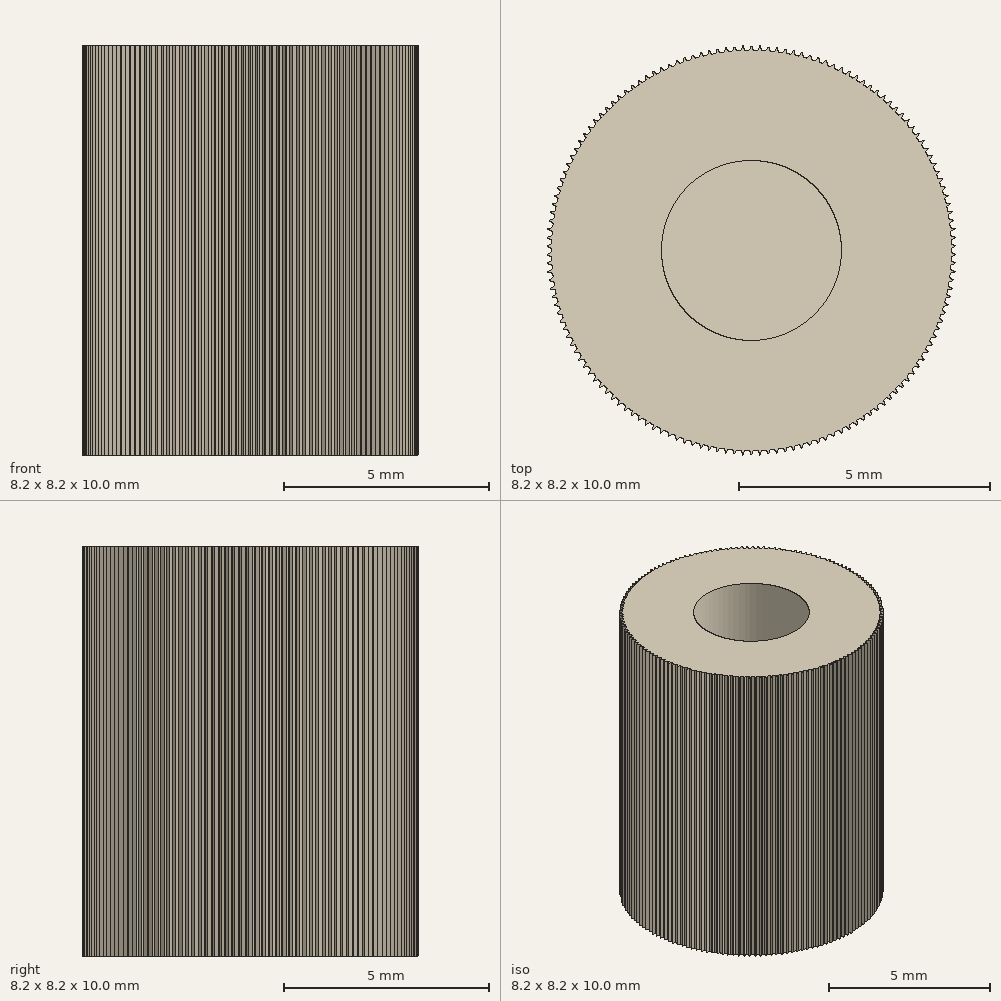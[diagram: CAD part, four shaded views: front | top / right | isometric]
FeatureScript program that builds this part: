
annotation { "Feature Type Name" : "Feature", "Feature Type Description" : "" }
export const myFeature = defineFeature(function(context is Context, id is Id, definition is map)
    precondition{}
    {
        {
            var Q0;
            Q0=qCreatedBy(makeId("Top.planeOp"),FACE);
            var sketch = newSketch(context, id + "F0", { "sketchPlane" : qUnion([Q0])});
            skArc(sketch, "E0", {"start": v(-0.04, 4) * mm, "mid": v(-0.08, 4) * mm, "end": v(-0.13, 4) * mm});
            skLineSegment(sketch, "E1", {"start": v(-0.04, 4) * mm, "end": v(0, 4.1) * mm});
            skLineSegment(sketch, "E2", {"start": v(0, 4.1) * mm, "end": v(0.04, 4) * mm});
            skLineSegment(sketch, "E3.1.0", {"start": v(-0.2, 4) * mm, "end": v(-0.17, 4.1) * mm});
            skLineSegment(sketch, "E3.1.1", {"start": v(-0.17, 4.1) * mm, "end": v(-0.13, 4) * mm});
            skLineSegment(sketch, "E3.2.0", {"start": v(-0.37, 3.98) * mm, "end": v(-0.34, 4.08) * mm});
            skLineSegment(sketch, "E3.2.1", {"start": v(-0.34, 4.08) * mm, "end": v(-0.3, 3.99) * mm});
            skLineSegment(sketch, "E3.3.0", {"start": v(-0.54, 3.96) * mm, "end": v(-0.51, 4.07) * mm});
            skLineSegment(sketch, "E3.3.1", {"start": v(-0.51, 4.07) * mm, "end": v(-0.46, 3.97) * mm});
            skLineSegment(sketch, "E3.4.0", {"start": v(-0.7, 3.94) * mm, "end": v(-0.68, 4.04) * mm});
            skLineSegment(sketch, "E3.4.1", {"start": v(-0.68, 4.04) * mm, "end": v(-0.63, 3.95) * mm});
            skLineSegment(sketch, "E3.5.0", {"start": v(-0.87, 3.9) * mm, "end": v(-0.85, 4) * mm});
            skLineSegment(sketch, "E3.5.1", {"start": v(-0.85, 4) * mm, "end": v(-0.8, 3.92) * mm});
            skLineSegment(sketch, "E3.6.0", {"start": v(-1.03, 3.86) * mm, "end": v(-1.02, 3.97) * mm});
            skLineSegment(sketch, "E3.6.1", {"start": v(-1.02, 3.97) * mm, "end": v(-0.96, 3.88) * mm});
            skLineSegment(sketch, "E3.7.0", {"start": v(-1.2, 3.82) * mm, "end": v(-1.18, 3.92) * mm});
            skLineSegment(sketch, "E3.7.1", {"start": v(-1.18, 3.92) * mm, "end": v(-1.12, 3.84) * mm});
            skLineSegment(sketch, "E3.8.0", {"start": v(-1.35, 3.76) * mm, "end": v(-1.35, 3.87) * mm});
            skLineSegment(sketch, "E3.8.1", {"start": v(-1.35, 3.87) * mm, "end": v(-1.28, 3.8) * mm});
            skLineSegment(sketch, "E3.9.0", {"start": v(-1.5, 3.7) * mm, "end": v(-1.5, 3.81) * mm});
            skLineSegment(sketch, "E3.9.1", {"start": v(-1.5, 3.81) * mm, "end": v(-1.43, 3.73) * mm});
            skLineSegment(sketch, "E3.10.0", {"start": v(-1.66, 3.64) * mm, "end": v(-1.67, 3.74) * mm});
            skLineSegment(sketch, "E3.10.1", {"start": v(-1.67, 3.74) * mm, "end": v(-1.59, 3.67) * mm});
            skLineSegment(sketch, "E3.11.0", {"start": v(-1.81, 3.56) * mm, "end": v(-1.82, 3.67) * mm});
            skLineSegment(sketch, "E3.11.1", {"start": v(-1.82, 3.67) * mm, "end": v(-1.74, 3.6) * mm});
            skLineSegment(sketch, "E3.12.0", {"start": v(-1.96, 3.49) * mm, "end": v(-1.97, 3.6) * mm});
            skLineSegment(sketch, "E3.12.1", {"start": v(-1.97, 3.6) * mm, "end": v(-1.9, 3.52) * mm});
            skLineSegment(sketch, "E3.13.0", {"start": v(-2.1, 3.4) * mm, "end": v(-2.12, 3.5) * mm});
            skLineSegment(sketch, "E3.13.1", {"start": v(-2.12, 3.5) * mm, "end": v(-2.04, 3.44) * mm});
            skLineSegment(sketch, "E3.14.0", {"start": v(-2.25, 3.3) * mm, "end": v(-2.27, 3.41) * mm});
            skLineSegment(sketch, "E3.14.1", {"start": v(-2.27, 3.41) * mm, "end": v(-2.18, 3.35) * mm});
            skLineSegment(sketch, "E3.15.0", {"start": v(-2.38, 3.21) * mm, "end": v(-2.4, 3.32) * mm});
            skLineSegment(sketch, "E3.15.1", {"start": v(-2.4, 3.32) * mm, "end": v(-2.32, 3.26) * mm});
            skLineSegment(sketch, "E3.16.0", {"start": v(-2.52, 3.1) * mm, "end": v(-2.55, 3.21) * mm});
            skLineSegment(sketch, "E3.16.1", {"start": v(-2.55, 3.21) * mm, "end": v(-2.45, 3.16) * mm});
            skLineSegment(sketch, "E3.17.0", {"start": v(-2.64, 3) * mm, "end": v(-2.68, 3.1) * mm});
            skLineSegment(sketch, "E3.17.1", {"start": v(-2.68, 3.1) * mm, "end": v(-2.58, 3.05) * mm});
            skLineSegment(sketch, "E3.18.0", {"start": v(-2.77, 2.89) * mm, "end": v(-2.8, 2.99) * mm});
            skLineSegment(sketch, "E3.18.1", {"start": v(-2.8, 2.99) * mm, "end": v(-2.7, 2.94) * mm});
            skLineSegment(sketch, "E3.19.0", {"start": v(-2.89, 2.77) * mm, "end": v(-2.93, 2.87) * mm});
            skLineSegment(sketch, "E3.19.1", {"start": v(-2.93, 2.87) * mm, "end": v(-2.83, 2.83) * mm});
            skLineSegment(sketch, "E3.20.0", {"start": v(-3, 2.65) * mm, "end": v(-3.05, 2.74) * mm});
            skLineSegment(sketch, "E3.20.1", {"start": v(-3.05, 2.74) * mm, "end": v(-2.95, 2.7) * mm});
            skLineSegment(sketch, "E3.21.0", {"start": v(-3.1, 2.52) * mm, "end": v(-3.16, 2.61) * mm});
            skLineSegment(sketch, "E3.21.1", {"start": v(-3.16, 2.61) * mm, "end": v(-3.06, 2.58) * mm});
            skLineSegment(sketch, "E3.22.0", {"start": v(-3.21, 2.39) * mm, "end": v(-3.26, 2.48) * mm});
            skLineSegment(sketch, "E3.22.1", {"start": v(-3.26, 2.48) * mm, "end": v(-3.16, 2.45) * mm});
            skLineSegment(sketch, "E3.23.0", {"start": v(-3.3, 2.25) * mm, "end": v(-3.37, 2.34) * mm});
            skLineSegment(sketch, "E3.23.1", {"start": v(-3.37, 2.34) * mm, "end": v(-3.26, 2.32) * mm});
            skLineSegment(sketch, "E3.24.0", {"start": v(-3.4, 2.1) * mm, "end": v(-3.46, 2.2) * mm});
            skLineSegment(sketch, "E3.24.1", {"start": v(-3.46, 2.2) * mm, "end": v(-3.36, 2.18) * mm});
            skLineSegment(sketch, "E3.25.0", {"start": v(-3.48, 1.97) * mm, "end": v(-3.55, 2.05) * mm});
            skLineSegment(sketch, "E3.25.1", {"start": v(-3.55, 2.05) * mm, "end": v(-3.44, 2.04) * mm});
            skLineSegment(sketch, "E3.26.0", {"start": v(-3.56, 1.82) * mm, "end": v(-3.63, 1.9) * mm});
            skLineSegment(sketch, "E3.26.1", {"start": v(-3.63, 1.9) * mm, "end": v(-3.53, 1.89) * mm});
            skLineSegment(sketch, "E3.27.0", {"start": v(-3.64, 1.67) * mm, "end": v(-3.7, 1.75) * mm});
            skLineSegment(sketch, "E3.27.1", {"start": v(-3.7, 1.75) * mm, "end": v(-3.6, 1.74) * mm});
            skLineSegment(sketch, "E3.28.0", {"start": v(-3.7, 1.51) * mm, "end": v(-3.78, 1.59) * mm});
            skLineSegment(sketch, "E3.28.1", {"start": v(-3.78, 1.59) * mm, "end": v(-3.67, 1.59) * mm});
            skLineSegment(sketch, "E3.29.0", {"start": v(-3.76, 1.36) * mm, "end": v(-3.84, 1.43) * mm});
            skLineSegment(sketch, "E3.29.1", {"start": v(-3.84, 1.43) * mm, "end": v(-3.73, 1.43) * mm});
            skLineSegment(sketch, "E3.30.0", {"start": v(-3.82, 1.2) * mm, "end": v(-3.9, 1.27) * mm});
            skLineSegment(sketch, "E3.30.1", {"start": v(-3.9, 1.27) * mm, "end": v(-3.8, 1.27) * mm});
            skLineSegment(sketch, "E3.31.0", {"start": v(-3.86, 1.04) * mm, "end": v(-3.95, 1.1) * mm});
            skLineSegment(sketch, "E3.31.1", {"start": v(-3.95, 1.1) * mm, "end": v(-3.84, 1.11) * mm});
            skLineSegment(sketch, "E3.32.0", {"start": v(-3.9, 0.87) * mm, "end": v(-4, 0.94) * mm});
            skLineSegment(sketch, "E3.32.1", {"start": v(-4, 0.94) * mm, "end": v(-3.88, 0.95) * mm});
            skLineSegment(sketch, "E3.33.0", {"start": v(-3.94, 0.71) * mm, "end": v(-4.03, 0.77) * mm});
            skLineSegment(sketch, "E3.33.1", {"start": v(-4.03, 0.77) * mm, "end": v(-3.92, 0.79) * mm});
            skLineSegment(sketch, "E3.34.0", {"start": v(-3.96, 0.54) * mm, "end": v(-4.05, 0.6) * mm});
            skLineSegment(sketch, "E3.34.1", {"start": v(-4.05, 0.6) * mm, "end": v(-3.95, 0.62) * mm});
            skLineSegment(sketch, "E3.35.0", {"start": v(-3.98, 0.38) * mm, "end": v(-4.08, 0.43) * mm});
            skLineSegment(sketch, "E3.35.1", {"start": v(-4.08, 0.43) * mm, "end": v(-3.97, 0.46) * mm});
            skLineSegment(sketch, "E3.36.0", {"start": v(-4, 0.21) * mm, "end": v(-4.1, 0.26) * mm});
            skLineSegment(sketch, "E3.36.1", {"start": v(-4.1, 0.26) * mm, "end": v(-3.99, 0.3) * mm});
            skLineSegment(sketch, "E3.37.0", {"start": v(-4, 0.04) * mm, "end": v(-4.1, 0.09) * mm});
            skLineSegment(sketch, "E3.37.1", {"start": v(-4.1, 0.09) * mm, "end": v(-4, 0.12) * mm});
            skLineSegment(sketch, "E3.38.0", {"start": v(-4, -0.12) * mm, "end": v(-4.1, -0.09) * mm});
            skLineSegment(sketch, "E3.38.1", {"start": v(-4.1, -0.09) * mm, "end": v(-4, -0.04) * mm});
            skLineSegment(sketch, "E3.39.0", {"start": v(-3.99, -0.3) * mm, "end": v(-4.1, -0.26) * mm});
            skLineSegment(sketch, "E3.39.1", {"start": v(-4.1, -0.26) * mm, "end": v(-4, -0.21) * mm});
            skLineSegment(sketch, "E3.40.0", {"start": v(-3.97, -0.46) * mm, "end": v(-4.08, -0.43) * mm});
            skLineSegment(sketch, "E3.40.1", {"start": v(-4.08, -0.43) * mm, "end": v(-3.98, -0.38) * mm});
            skLineSegment(sketch, "E3.41.0", {"start": v(-3.95, -0.62) * mm, "end": v(-4.05, -0.6) * mm});
            skLineSegment(sketch, "E3.41.1", {"start": v(-4.05, -0.6) * mm, "end": v(-3.96, -0.54) * mm});
            skLineSegment(sketch, "E3.42.0", {"start": v(-3.92, -0.79) * mm, "end": v(-4.03, -0.77) * mm});
            skLineSegment(sketch, "E3.42.1", {"start": v(-4.03, -0.77) * mm, "end": v(-3.94, -0.7) * mm});
            skLineSegment(sketch, "E3.43.0", {"start": v(-3.88, -0.95) * mm, "end": v(-4, -0.94) * mm});
            skLineSegment(sketch, "E3.43.1", {"start": v(-4, -0.94) * mm, "end": v(-3.9, -0.87) * mm});
            skLineSegment(sketch, "E3.44.0", {"start": v(-3.84, -1.11) * mm, "end": v(-3.95, -1.1) * mm});
            skLineSegment(sketch, "E3.44.1", {"start": v(-3.95, -1.1) * mm, "end": v(-3.86, -1.04) * mm});
            skLineSegment(sketch, "E3.45.0", {"start": v(-3.8, -1.27) * mm, "end": v(-3.9, -1.27) * mm});
            skLineSegment(sketch, "E3.45.1", {"start": v(-3.9, -1.27) * mm, "end": v(-3.82, -1.2) * mm});
            skLineSegment(sketch, "E3.46.0", {"start": v(-3.73, -1.43) * mm, "end": v(-3.84, -1.43) * mm});
            skLineSegment(sketch, "E3.46.1", {"start": v(-3.84, -1.43) * mm, "end": v(-3.76, -1.36) * mm});
            skLineSegment(sketch, "E3.47.0", {"start": v(-3.67, -1.59) * mm, "end": v(-3.78, -1.59) * mm});
            skLineSegment(sketch, "E3.47.1", {"start": v(-3.78, -1.59) * mm, "end": v(-3.7, -1.51) * mm});
            skLineSegment(sketch, "E3.48.0", {"start": v(-3.6, -1.74) * mm, "end": v(-3.7, -1.75) * mm});
            skLineSegment(sketch, "E3.48.1", {"start": v(-3.7, -1.75) * mm, "end": v(-3.64, -1.67) * mm});
            skLineSegment(sketch, "E3.49.0", {"start": v(-3.53, -1.89) * mm, "end": v(-3.63, -1.9) * mm});
            skLineSegment(sketch, "E3.49.1", {"start": v(-3.63, -1.9) * mm, "end": v(-3.56, -1.82) * mm});
            skLineSegment(sketch, "E3.50.0", {"start": v(-3.44, -2.03) * mm, "end": v(-3.55, -2.05) * mm});
            skLineSegment(sketch, "E3.50.1", {"start": v(-3.55, -2.05) * mm, "end": v(-3.48, -1.96) * mm});
            skLineSegment(sketch, "E3.51.0", {"start": v(-3.36, -2.18) * mm, "end": v(-3.46, -2.2) * mm});
            skLineSegment(sketch, "E3.51.1", {"start": v(-3.46, -2.2) * mm, "end": v(-3.4, -2.1) * mm});
            skLineSegment(sketch, "E3.52.0", {"start": v(-3.26, -2.32) * mm, "end": v(-3.37, -2.34) * mm});
            skLineSegment(sketch, "E3.52.1", {"start": v(-3.37, -2.34) * mm, "end": v(-3.3, -2.25) * mm});
            skLineSegment(sketch, "E3.53.0", {"start": v(-3.16, -2.45) * mm, "end": v(-3.26, -2.48) * mm});
            skLineSegment(sketch, "E3.53.1", {"start": v(-3.26, -2.48) * mm, "end": v(-3.21, -2.39) * mm});
            skLineSegment(sketch, "E3.54.0", {"start": v(-3.06, -2.58) * mm, "end": v(-3.16, -2.61) * mm});
            skLineSegment(sketch, "E3.54.1", {"start": v(-3.16, -2.61) * mm, "end": v(-3.1, -2.52) * mm});
            skLineSegment(sketch, "E3.55.0", {"start": v(-2.95, -2.7) * mm, "end": v(-3.05, -2.74) * mm});
            skLineSegment(sketch, "E3.55.1", {"start": v(-3.05, -2.74) * mm, "end": v(-3, -2.65) * mm});
            skLineSegment(sketch, "E3.56.0", {"start": v(-2.83, -2.83) * mm, "end": v(-2.93, -2.87) * mm});
            skLineSegment(sketch, "E3.56.1", {"start": v(-2.93, -2.87) * mm, "end": v(-2.89, -2.77) * mm});
            skLineSegment(sketch, "E3.57.0", {"start": v(-2.7, -2.94) * mm, "end": v(-2.8, -2.99) * mm});
            skLineSegment(sketch, "E3.57.1", {"start": v(-2.8, -2.99) * mm, "end": v(-2.77, -2.89) * mm});
            skLineSegment(sketch, "E3.58.0", {"start": v(-2.58, -3.05) * mm, "end": v(-2.68, -3.1) * mm});
            skLineSegment(sketch, "E3.58.1", {"start": v(-2.68, -3.1) * mm, "end": v(-2.64, -3) * mm});
            skLineSegment(sketch, "E3.59.0", {"start": v(-2.45, -3.16) * mm, "end": v(-2.55, -3.21) * mm});
            skLineSegment(sketch, "E3.59.1", {"start": v(-2.55, -3.21) * mm, "end": v(-2.52, -3.1) * mm});
            skLineSegment(sketch, "E3.60.0", {"start": v(-2.32, -3.26) * mm, "end": v(-2.4, -3.32) * mm});
            skLineSegment(sketch, "E3.60.1", {"start": v(-2.4, -3.32) * mm, "end": v(-2.38, -3.21) * mm});
            skLineSegment(sketch, "E3.61.0", {"start": v(-2.18, -3.35) * mm, "end": v(-2.27, -3.41) * mm});
            skLineSegment(sketch, "E3.61.1", {"start": v(-2.27, -3.41) * mm, "end": v(-2.25, -3.3) * mm});
            skLineSegment(sketch, "E3.62.0", {"start": v(-2.04, -3.44) * mm, "end": v(-2.12, -3.5) * mm});
            skLineSegment(sketch, "E3.62.1", {"start": v(-2.12, -3.5) * mm, "end": v(-2.1, -3.4) * mm});
            skLineSegment(sketch, "E3.63.0", {"start": v(-1.9, -3.52) * mm, "end": v(-1.97, -3.6) * mm});
            skLineSegment(sketch, "E3.63.1", {"start": v(-1.97, -3.6) * mm, "end": v(-1.96, -3.49) * mm});
            skLineSegment(sketch, "E3.64.0", {"start": v(-1.74, -3.6) * mm, "end": v(-1.82, -3.67) * mm});
            skLineSegment(sketch, "E3.64.1", {"start": v(-1.82, -3.67) * mm, "end": v(-1.81, -3.56) * mm});
            skLineSegment(sketch, "E3.65.0", {"start": v(-1.6, -3.67) * mm, "end": v(-1.67, -3.74) * mm});
            skLineSegment(sketch, "E3.65.1", {"start": v(-1.67, -3.74) * mm, "end": v(-1.66, -3.64) * mm});
            skLineSegment(sketch, "E3.66.0", {"start": v(-1.44, -3.73) * mm, "end": v(-1.5, -3.81) * mm});
            skLineSegment(sketch, "E3.66.1", {"start": v(-1.5, -3.81) * mm, "end": v(-1.51, -3.7) * mm});
            skLineSegment(sketch, "E3.67.0", {"start": v(-1.28, -3.8) * mm, "end": v(-1.35, -3.87) * mm});
            skLineSegment(sketch, "E3.67.1", {"start": v(-1.35, -3.87) * mm, "end": v(-1.35, -3.76) * mm});
            skLineSegment(sketch, "E3.68.0", {"start": v(-1.12, -3.84) * mm, "end": v(-1.18, -3.92) * mm});
            skLineSegment(sketch, "E3.68.1", {"start": v(-1.18, -3.92) * mm, "end": v(-1.2, -3.82) * mm});
            skLineSegment(sketch, "E3.69.0", {"start": v(-0.96, -3.88) * mm, "end": v(-1.02, -3.97) * mm});
            skLineSegment(sketch, "E3.69.1", {"start": v(-1.02, -3.97) * mm, "end": v(-1.03, -3.86) * mm});
            skLineSegment(sketch, "E3.70.0", {"start": v(-0.8, -3.92) * mm, "end": v(-0.85, -4) * mm});
            skLineSegment(sketch, "E3.70.1", {"start": v(-0.85, -4) * mm, "end": v(-0.87, -3.9) * mm});
            skLineSegment(sketch, "E3.71.0", {"start": v(-0.63, -3.95) * mm, "end": v(-0.68, -4.04) * mm});
            skLineSegment(sketch, "E3.71.1", {"start": v(-0.68, -4.04) * mm, "end": v(-0.7, -3.94) * mm});
            skLineSegment(sketch, "E3.72.0", {"start": v(-0.46, -3.97) * mm, "end": v(-0.51, -4.07) * mm});
            skLineSegment(sketch, "E3.72.1", {"start": v(-0.51, -4.07) * mm, "end": v(-0.54, -3.96) * mm});
            skLineSegment(sketch, "E3.73.0", {"start": v(-0.3, -3.99) * mm, "end": v(-0.34, -4.08) * mm});
            skLineSegment(sketch, "E3.73.1", {"start": v(-0.34, -4.08) * mm, "end": v(-0.38, -3.98) * mm});
            skLineSegment(sketch, "E3.74.0", {"start": v(-0.13, -4) * mm, "end": v(-0.17, -4.1) * mm});
            skLineSegment(sketch, "E3.74.1", {"start": v(-0.17, -4.1) * mm, "end": v(-0.2, -4) * mm});
            skLineSegment(sketch, "E3.75.0", {"start": v(0.04, -4) * mm, "end": v(0, -4.1) * mm});
            skLineSegment(sketch, "E3.75.1", {"start": v(0, -4.1) * mm, "end": v(-0.04, -4) * mm});
            skLineSegment(sketch, "E3.76.0", {"start": v(0.2, -4) * mm, "end": v(0.17, -4.1) * mm});
            skLineSegment(sketch, "E3.76.1", {"start": v(0.17, -4.1) * mm, "end": v(0.13, -4) * mm});
            skLineSegment(sketch, "E3.77.0", {"start": v(0.37, -3.98) * mm, "end": v(0.34, -4.08) * mm});
            skLineSegment(sketch, "E3.77.1", {"start": v(0.34, -4.08) * mm, "end": v(0.3, -3.99) * mm});
            skLineSegment(sketch, "E3.78.0", {"start": v(0.54, -3.96) * mm, "end": v(0.51, -4.07) * mm});
            skLineSegment(sketch, "E3.78.1", {"start": v(0.51, -4.07) * mm, "end": v(0.46, -3.97) * mm});
            skLineSegment(sketch, "E3.79.0", {"start": v(0.7, -3.94) * mm, "end": v(0.68, -4.04) * mm});
            skLineSegment(sketch, "E3.79.1", {"start": v(0.68, -4.04) * mm, "end": v(0.63, -3.95) * mm});
            skLineSegment(sketch, "E3.80.0", {"start": v(0.87, -3.9) * mm, "end": v(0.85, -4) * mm});
            skLineSegment(sketch, "E3.80.1", {"start": v(0.85, -4) * mm, "end": v(0.8, -3.92) * mm});
            skLineSegment(sketch, "E3.81.0", {"start": v(1.03, -3.86) * mm, "end": v(1.02, -3.97) * mm});
            skLineSegment(sketch, "E3.81.1", {"start": v(1.02, -3.97) * mm, "end": v(0.96, -3.88) * mm});
            skLineSegment(sketch, "E3.82.0", {"start": v(1.2, -3.82) * mm, "end": v(1.18, -3.92) * mm});
            skLineSegment(sketch, "E3.82.1", {"start": v(1.18, -3.92) * mm, "end": v(1.12, -3.84) * mm});
            skLineSegment(sketch, "E3.83.0", {"start": v(1.35, -3.76) * mm, "end": v(1.35, -3.87) * mm});
            skLineSegment(sketch, "E3.83.1", {"start": v(1.35, -3.87) * mm, "end": v(1.28, -3.8) * mm});
            skLineSegment(sketch, "E3.84.0", {"start": v(1.5, -3.7) * mm, "end": v(1.5, -3.81) * mm});
            skLineSegment(sketch, "E3.84.1", {"start": v(1.5, -3.81) * mm, "end": v(1.43, -3.73) * mm});
            skLineSegment(sketch, "E3.85.0", {"start": v(1.66, -3.64) * mm, "end": v(1.67, -3.74) * mm});
            skLineSegment(sketch, "E3.85.1", {"start": v(1.67, -3.74) * mm, "end": v(1.59, -3.67) * mm});
            skLineSegment(sketch, "E3.86.0", {"start": v(1.81, -3.56) * mm, "end": v(1.82, -3.67) * mm});
            skLineSegment(sketch, "E3.86.1", {"start": v(1.82, -3.67) * mm, "end": v(1.74, -3.6) * mm});
            skLineSegment(sketch, "E3.87.0", {"start": v(1.96, -3.49) * mm, "end": v(1.97, -3.6) * mm});
            skLineSegment(sketch, "E3.87.1", {"start": v(1.97, -3.6) * mm, "end": v(1.9, -3.52) * mm});
            skLineSegment(sketch, "E3.88.0", {"start": v(2.1, -3.4) * mm, "end": v(2.12, -3.5) * mm});
            skLineSegment(sketch, "E3.88.1", {"start": v(2.12, -3.5) * mm, "end": v(2.04, -3.44) * mm});
            skLineSegment(sketch, "E3.89.0", {"start": v(2.25, -3.3) * mm, "end": v(2.27, -3.41) * mm});
            skLineSegment(sketch, "E3.89.1", {"start": v(2.27, -3.41) * mm, "end": v(2.18, -3.35) * mm});
            skLineSegment(sketch, "E3.90.0", {"start": v(2.38, -3.21) * mm, "end": v(2.4, -3.32) * mm});
            skLineSegment(sketch, "E3.90.1", {"start": v(2.4, -3.32) * mm, "end": v(2.32, -3.26) * mm});
            skLineSegment(sketch, "E3.91.0", {"start": v(2.52, -3.1) * mm, "end": v(2.55, -3.21) * mm});
            skLineSegment(sketch, "E3.91.1", {"start": v(2.55, -3.21) * mm, "end": v(2.45, -3.16) * mm});
            skLineSegment(sketch, "E3.92.0", {"start": v(2.64, -3) * mm, "end": v(2.68, -3.1) * mm});
            skLineSegment(sketch, "E3.92.1", {"start": v(2.68, -3.1) * mm, "end": v(2.58, -3.05) * mm});
            skLineSegment(sketch, "E3.93.0", {"start": v(2.77, -2.89) * mm, "end": v(2.8, -2.99) * mm});
            skLineSegment(sketch, "E3.93.1", {"start": v(2.8, -2.99) * mm, "end": v(2.7, -2.94) * mm});
            skLineSegment(sketch, "E3.94.0", {"start": v(2.89, -2.77) * mm, "end": v(2.93, -2.87) * mm});
            skLineSegment(sketch, "E3.94.1", {"start": v(2.93, -2.87) * mm, "end": v(2.83, -2.83) * mm});
            skLineSegment(sketch, "E3.95.0", {"start": v(3, -2.65) * mm, "end": v(3.05, -2.74) * mm});
            skLineSegment(sketch, "E3.95.1", {"start": v(3.05, -2.74) * mm, "end": v(2.95, -2.7) * mm});
            skLineSegment(sketch, "E3.96.0", {"start": v(3.1, -2.52) * mm, "end": v(3.16, -2.61) * mm});
            skLineSegment(sketch, "E3.96.1", {"start": v(3.16, -2.61) * mm, "end": v(3.06, -2.58) * mm});
            skLineSegment(sketch, "E3.97.0", {"start": v(3.21, -2.39) * mm, "end": v(3.26, -2.48) * mm});
            skLineSegment(sketch, "E3.97.1", {"start": v(3.26, -2.48) * mm, "end": v(3.16, -2.45) * mm});
            skLineSegment(sketch, "E3.98.0", {"start": v(3.3, -2.25) * mm, "end": v(3.37, -2.34) * mm});
            skLineSegment(sketch, "E3.98.1", {"start": v(3.37, -2.34) * mm, "end": v(3.26, -2.32) * mm});
            skLineSegment(sketch, "E3.99.0", {"start": v(3.4, -2.1) * mm, "end": v(3.46, -2.2) * mm});
            skLineSegment(sketch, "E3.99.1", {"start": v(3.46, -2.2) * mm, "end": v(3.36, -2.18) * mm});
            skLineSegment(sketch, "E3.100.0", {"start": v(3.48, -1.97) * mm, "end": v(3.55, -2.05) * mm});
            skLineSegment(sketch, "E3.100.1", {"start": v(3.55, -2.05) * mm, "end": v(3.44, -2.04) * mm});
            skLineSegment(sketch, "E3.101.0", {"start": v(3.56, -1.82) * mm, "end": v(3.63, -1.9) * mm});
            skLineSegment(sketch, "E3.101.1", {"start": v(3.63, -1.9) * mm, "end": v(3.53, -1.89) * mm});
            skLineSegment(sketch, "E3.102.0", {"start": v(3.64, -1.67) * mm, "end": v(3.7, -1.75) * mm});
            skLineSegment(sketch, "E3.102.1", {"start": v(3.7, -1.75) * mm, "end": v(3.6, -1.74) * mm});
            skLineSegment(sketch, "E3.103.0", {"start": v(3.7, -1.51) * mm, "end": v(3.78, -1.59) * mm});
            skLineSegment(sketch, "E3.103.1", {"start": v(3.78, -1.59) * mm, "end": v(3.67, -1.59) * mm});
            skLineSegment(sketch, "E3.104.0", {"start": v(3.76, -1.36) * mm, "end": v(3.84, -1.43) * mm});
            skLineSegment(sketch, "E3.104.1", {"start": v(3.84, -1.43) * mm, "end": v(3.73, -1.43) * mm});
            skLineSegment(sketch, "E3.105.0", {"start": v(3.82, -1.2) * mm, "end": v(3.9, -1.27) * mm});
            skLineSegment(sketch, "E3.105.1", {"start": v(3.9, -1.27) * mm, "end": v(3.8, -1.27) * mm});
            skLineSegment(sketch, "E3.106.0", {"start": v(3.86, -1.04) * mm, "end": v(3.95, -1.1) * mm});
            skLineSegment(sketch, "E3.106.1", {"start": v(3.95, -1.1) * mm, "end": v(3.84, -1.11) * mm});
            skLineSegment(sketch, "E3.107.0", {"start": v(3.9, -0.87) * mm, "end": v(4, -0.94) * mm});
            skLineSegment(sketch, "E3.107.1", {"start": v(4, -0.94) * mm, "end": v(3.88, -0.95) * mm});
            skLineSegment(sketch, "E3.108.0", {"start": v(3.94, -0.71) * mm, "end": v(4.03, -0.77) * mm});
            skLineSegment(sketch, "E3.108.1", {"start": v(4.03, -0.77) * mm, "end": v(3.92, -0.79) * mm});
            skLineSegment(sketch, "E3.109.0", {"start": v(3.96, -0.54) * mm, "end": v(4.05, -0.6) * mm});
            skLineSegment(sketch, "E3.109.1", {"start": v(4.05, -0.6) * mm, "end": v(3.95, -0.62) * mm});
            skLineSegment(sketch, "E3.110.0", {"start": v(3.98, -0.38) * mm, "end": v(4.08, -0.43) * mm});
            skLineSegment(sketch, "E3.110.1", {"start": v(4.08, -0.43) * mm, "end": v(3.97, -0.46) * mm});
            skLineSegment(sketch, "E3.111.0", {"start": v(4, -0.21) * mm, "end": v(4.1, -0.26) * mm});
            skLineSegment(sketch, "E3.111.1", {"start": v(4.1, -0.26) * mm, "end": v(3.99, -0.3) * mm});
            skLineSegment(sketch, "E3.112.0", {"start": v(4, -0.04) * mm, "end": v(4.1, -0.09) * mm});
            skLineSegment(sketch, "E3.112.1", {"start": v(4.1, -0.09) * mm, "end": v(4, -0.12) * mm});
            skLineSegment(sketch, "E3.113.0", {"start": v(4, 0.12) * mm, "end": v(4.1, 0.09) * mm});
            skLineSegment(sketch, "E3.113.1", {"start": v(4.1, 0.09) * mm, "end": v(4, 0.04) * mm});
            skLineSegment(sketch, "E3.114.0", {"start": v(3.99, 0.3) * mm, "end": v(4.1, 0.26) * mm});
            skLineSegment(sketch, "E3.114.1", {"start": v(4.1, 0.26) * mm, "end": v(4, 0.21) * mm});
            skLineSegment(sketch, "E3.115.0", {"start": v(3.97, 0.46) * mm, "end": v(4.08, 0.43) * mm});
            skLineSegment(sketch, "E3.115.1", {"start": v(4.08, 0.43) * mm, "end": v(3.98, 0.38) * mm});
            skLineSegment(sketch, "E3.116.0", {"start": v(3.95, 0.62) * mm, "end": v(4.05, 0.6) * mm});
            skLineSegment(sketch, "E3.116.1", {"start": v(4.05, 0.6) * mm, "end": v(3.96, 0.54) * mm});
            skLineSegment(sketch, "E3.117.0", {"start": v(3.92, 0.79) * mm, "end": v(4.03, 0.77) * mm});
            skLineSegment(sketch, "E3.117.1", {"start": v(4.03, 0.77) * mm, "end": v(3.94, 0.7) * mm});
            skLineSegment(sketch, "E3.118.0", {"start": v(3.88, 0.95) * mm, "end": v(4, 0.94) * mm});
            skLineSegment(sketch, "E3.118.1", {"start": v(4, 0.94) * mm, "end": v(3.9, 0.87) * mm});
            skLineSegment(sketch, "E3.119.0", {"start": v(3.84, 1.11) * mm, "end": v(3.95, 1.1) * mm});
            skLineSegment(sketch, "E3.119.1", {"start": v(3.95, 1.1) * mm, "end": v(3.86, 1.04) * mm});
            skLineSegment(sketch, "E3.120.0", {"start": v(3.8, 1.27) * mm, "end": v(3.9, 1.27) * mm});
            skLineSegment(sketch, "E3.120.1", {"start": v(3.9, 1.27) * mm, "end": v(3.82, 1.2) * mm});
            skLineSegment(sketch, "E3.121.0", {"start": v(3.73, 1.43) * mm, "end": v(3.84, 1.43) * mm});
            skLineSegment(sketch, "E3.121.1", {"start": v(3.84, 1.43) * mm, "end": v(3.76, 1.36) * mm});
            skLineSegment(sketch, "E3.122.0", {"start": v(3.67, 1.59) * mm, "end": v(3.78, 1.59) * mm});
            skLineSegment(sketch, "E3.122.1", {"start": v(3.78, 1.59) * mm, "end": v(3.7, 1.51) * mm});
            skLineSegment(sketch, "E3.123.0", {"start": v(3.6, 1.74) * mm, "end": v(3.7, 1.75) * mm});
            skLineSegment(sketch, "E3.123.1", {"start": v(3.7, 1.75) * mm, "end": v(3.64, 1.67) * mm});
            skLineSegment(sketch, "E3.124.0", {"start": v(3.53, 1.89) * mm, "end": v(3.63, 1.9) * mm});
            skLineSegment(sketch, "E3.124.1", {"start": v(3.63, 1.9) * mm, "end": v(3.56, 1.82) * mm});
            skLineSegment(sketch, "E3.125.0", {"start": v(3.44, 2.03) * mm, "end": v(3.55, 2.05) * mm});
            skLineSegment(sketch, "E3.125.1", {"start": v(3.55, 2.05) * mm, "end": v(3.48, 1.96) * mm});
            skLineSegment(sketch, "E3.126.0", {"start": v(3.36, 2.18) * mm, "end": v(3.46, 2.2) * mm});
            skLineSegment(sketch, "E3.126.1", {"start": v(3.46, 2.2) * mm, "end": v(3.4, 2.1) * mm});
            skLineSegment(sketch, "E3.127.0", {"start": v(3.26, 2.32) * mm, "end": v(3.37, 2.34) * mm});
            skLineSegment(sketch, "E3.127.1", {"start": v(3.37, 2.34) * mm, "end": v(3.3, 2.25) * mm});
            skLineSegment(sketch, "E3.128.0", {"start": v(3.16, 2.45) * mm, "end": v(3.26, 2.48) * mm});
            skLineSegment(sketch, "E3.128.1", {"start": v(3.26, 2.48) * mm, "end": v(3.21, 2.39) * mm});
            skLineSegment(sketch, "E3.129.0", {"start": v(3.06, 2.58) * mm, "end": v(3.16, 2.61) * mm});
            skLineSegment(sketch, "E3.129.1", {"start": v(3.16, 2.61) * mm, "end": v(3.1, 2.52) * mm});
            skLineSegment(sketch, "E3.130.0", {"start": v(2.95, 2.7) * mm, "end": v(3.05, 2.74) * mm});
            skLineSegment(sketch, "E3.130.1", {"start": v(3.05, 2.74) * mm, "end": v(3, 2.65) * mm});
            skLineSegment(sketch, "E3.131.0", {"start": v(2.83, 2.83) * mm, "end": v(2.93, 2.87) * mm});
            skLineSegment(sketch, "E3.131.1", {"start": v(2.93, 2.87) * mm, "end": v(2.89, 2.77) * mm});
            skLineSegment(sketch, "E3.132.0", {"start": v(2.7, 2.94) * mm, "end": v(2.8, 2.99) * mm});
            skLineSegment(sketch, "E3.132.1", {"start": v(2.8, 2.99) * mm, "end": v(2.77, 2.89) * mm});
            skLineSegment(sketch, "E3.133.0", {"start": v(2.58, 3.05) * mm, "end": v(2.68, 3.1) * mm});
            skLineSegment(sketch, "E3.133.1", {"start": v(2.68, 3.1) * mm, "end": v(2.64, 3) * mm});
            skLineSegment(sketch, "E3.134.0", {"start": v(2.45, 3.16) * mm, "end": v(2.55, 3.21) * mm});
            skLineSegment(sketch, "E3.134.1", {"start": v(2.55, 3.21) * mm, "end": v(2.52, 3.1) * mm});
            skLineSegment(sketch, "E3.135.0", {"start": v(2.32, 3.26) * mm, "end": v(2.4, 3.32) * mm});
            skLineSegment(sketch, "E3.135.1", {"start": v(2.4, 3.32) * mm, "end": v(2.38, 3.21) * mm});
            skLineSegment(sketch, "E3.136.0", {"start": v(2.18, 3.35) * mm, "end": v(2.27, 3.41) * mm});
            skLineSegment(sketch, "E3.136.1", {"start": v(2.27, 3.41) * mm, "end": v(2.25, 3.3) * mm});
            skLineSegment(sketch, "E3.137.0", {"start": v(2.04, 3.44) * mm, "end": v(2.12, 3.5) * mm});
            skLineSegment(sketch, "E3.137.1", {"start": v(2.12, 3.5) * mm, "end": v(2.1, 3.4) * mm});
            skLineSegment(sketch, "E3.138.0", {"start": v(1.9, 3.52) * mm, "end": v(1.97, 3.6) * mm});
            skLineSegment(sketch, "E3.138.1", {"start": v(1.97, 3.6) * mm, "end": v(1.96, 3.49) * mm});
            skLineSegment(sketch, "E3.139.0", {"start": v(1.74, 3.6) * mm, "end": v(1.82, 3.67) * mm});
            skLineSegment(sketch, "E3.139.1", {"start": v(1.82, 3.67) * mm, "end": v(1.81, 3.56) * mm});
            skLineSegment(sketch, "E3.140.0", {"start": v(1.6, 3.67) * mm, "end": v(1.67, 3.74) * mm});
            skLineSegment(sketch, "E3.140.1", {"start": v(1.67, 3.74) * mm, "end": v(1.66, 3.64) * mm});
            skLineSegment(sketch, "E3.141.0", {"start": v(1.44, 3.73) * mm, "end": v(1.5, 3.81) * mm});
            skLineSegment(sketch, "E3.141.1", {"start": v(1.5, 3.81) * mm, "end": v(1.51, 3.7) * mm});
            skLineSegment(sketch, "E3.142.0", {"start": v(1.28, 3.8) * mm, "end": v(1.35, 3.87) * mm});
            skLineSegment(sketch, "E3.142.1", {"start": v(1.35, 3.87) * mm, "end": v(1.35, 3.76) * mm});
            skLineSegment(sketch, "E3.143.0", {"start": v(1.12, 3.84) * mm, "end": v(1.18, 3.92) * mm});
            skLineSegment(sketch, "E3.143.1", {"start": v(1.18, 3.92) * mm, "end": v(1.2, 3.82) * mm});
            skLineSegment(sketch, "E3.144.0", {"start": v(0.96, 3.88) * mm, "end": v(1.02, 3.97) * mm});
            skLineSegment(sketch, "E3.144.1", {"start": v(1.02, 3.97) * mm, "end": v(1.03, 3.86) * mm});
            skLineSegment(sketch, "E3.145.0", {"start": v(0.8, 3.92) * mm, "end": v(0.85, 4) * mm});
            skLineSegment(sketch, "E3.145.1", {"start": v(0.85, 4) * mm, "end": v(0.87, 3.9) * mm});
            skLineSegment(sketch, "E3.146.0", {"start": v(0.63, 3.95) * mm, "end": v(0.68, 4.04) * mm});
            skLineSegment(sketch, "E3.146.1", {"start": v(0.68, 4.04) * mm, "end": v(0.7, 3.94) * mm});
            skLineSegment(sketch, "E3.147.0", {"start": v(0.46, 3.97) * mm, "end": v(0.51, 4.07) * mm});
            skLineSegment(sketch, "E3.147.1", {"start": v(0.51, 4.07) * mm, "end": v(0.54, 3.96) * mm});
            skLineSegment(sketch, "E3.148.0", {"start": v(0.3, 3.99) * mm, "end": v(0.34, 4.08) * mm});
            skLineSegment(sketch, "E3.148.1", {"start": v(0.34, 4.08) * mm, "end": v(0.38, 3.98) * mm});
            skLineSegment(sketch, "E3.149.0", {"start": v(0.13, 4) * mm, "end": v(0.17, 4.1) * mm});
            skLineSegment(sketch, "E3.149.1", {"start": v(0.17, 4.1) * mm, "end": v(0.2, 4) * mm});
            skArc(sketch, "E4.trimOffspring", {"start": v(0.13, 4) * mm, "mid": v(0.08, 4) * mm, "end": v(0.04, 4) * mm});
            skArc(sketch, "E5.trimOffspring", {"start": v(0.3, 3.99) * mm, "mid": v(0.25, 4) * mm, "end": v(0.2, 4) * mm});
            skArc(sketch, "E6.trimOffspring", {"start": v(0.46, 3.97) * mm, "mid": v(0.42, 3.98) * mm, "end": v(0.38, 3.98) * mm});
            skArc(sketch, "E7.trimOffspring", {"start": v(0.63, 3.95) * mm, "mid": v(0.58, 3.96) * mm, "end": v(0.54, 3.96) * mm});
            skArc(sketch, "E8.trimOffspring", {"start": v(0.8, 3.92) * mm, "mid": v(0.75, 3.93) * mm, "end": v(0.7, 3.94) * mm});
            skArc(sketch, "E9.trimOffspring", {"start": v(0.96, 3.88) * mm, "mid": v(0.91, 3.9) * mm, "end": v(0.87, 3.9) * mm});
            skArc(sketch, "E10.trimOffspring", {"start": v(1.12, 3.84) * mm, "mid": v(1.08, 3.85) * mm, "end": v(1.03, 3.86) * mm});
            skArc(sketch, "E11.trimOffspring", {"start": v(1.28, 3.8) * mm, "mid": v(1.24, 3.8) * mm, "end": v(1.2, 3.82) * mm});
            skArc(sketch, "E12.trimOffspring", {"start": v(1.44, 3.73) * mm, "mid": v(1.4, 3.75) * mm, "end": v(1.35, 3.76) * mm});
            skArc(sketch, "E13.trimOffspring", {"start": v(1.6, 3.67) * mm, "mid": v(1.55, 3.69) * mm, "end": v(1.51, 3.7) * mm});
            skArc(sketch, "E14.trimOffspring", {"start": v(1.74, 3.6) * mm, "mid": v(1.7, 3.62) * mm, "end": v(1.66, 3.64) * mm});
            skArc(sketch, "E15.trimOffspring", {"start": v(1.9, 3.52) * mm, "mid": v(1.85, 3.54) * mm, "end": v(1.81, 3.56) * mm});
            skArc(sketch, "E16.trimOffspring", {"start": v(2.04, 3.44) * mm, "mid": v(2, 3.46) * mm, "end": v(1.96, 3.49) * mm});
            skArc(sketch, "E17.trimOffspring", {"start": v(2.18, 3.35) * mm, "mid": v(2.14, 3.38) * mm, "end": v(2.1, 3.4) * mm});
            skArc(sketch, "E18.trimOffspring", {"start": v(2.32, 3.26) * mm, "mid": v(2.28, 3.28) * mm, "end": v(2.25, 3.3) * mm});
            skArc(sketch, "E19.trimOffspring", {"start": v(2.45, 3.16) * mm, "mid": v(2.42, 3.19) * mm, "end": v(2.38, 3.21) * mm});
            skArc(sketch, "E20.trimOffspring", {"start": v(2.58, 3.05) * mm, "mid": v(2.55, 3.08) * mm, "end": v(2.52, 3.1) * mm});
            skArc(sketch, "E21.trimOffspring", {"start": v(2.7, 2.94) * mm, "mid": v(2.68, 2.97) * mm, "end": v(2.64, 3) * mm});
            skArc(sketch, "E22.trimOffspring", {"start": v(2.83, 2.83) * mm, "mid": v(2.8, 2.86) * mm, "end": v(2.77, 2.89) * mm});
            skArc(sketch, "E23.trimOffspring", {"start": v(2.95, 2.7) * mm, "mid": v(2.92, 2.74) * mm, "end": v(2.89, 2.77) * mm});
            skArc(sketch, "E24.trimOffspring", {"start": v(3.06, 2.58) * mm, "mid": v(3.03, 2.61) * mm, "end": v(3, 2.65) * mm});
            skArc(sketch, "E25.trimOffspring", {"start": v(3.16, 2.45) * mm, "mid": v(3.13, 2.48) * mm, "end": v(3.1, 2.52) * mm});
            skArc(sketch, "E26.trimOffspring", {"start": v(3.26, 2.32) * mm, "mid": v(3.24, 2.35) * mm, "end": v(3.21, 2.39) * mm});
            skArc(sketch, "E27.trimOffspring", {"start": v(3.36, 2.18) * mm, "mid": v(3.33, 2.21) * mm, "end": v(3.3, 2.25) * mm});
            skArc(sketch, "E28.trimOffspring", {"start": v(3.44, 2.03) * mm, "mid": v(3.42, 2.07) * mm, "end": v(3.4, 2.1) * mm});
            skArc(sketch, "E29.trimOffspring", {"start": v(3.53, 1.89) * mm, "mid": v(3.5, 1.93) * mm, "end": v(3.48, 1.96) * mm});
            skArc(sketch, "E30.trimOffspring", {"start": v(3.6, 1.74) * mm, "mid": v(3.58, 1.78) * mm, "end": v(3.56, 1.82) * mm});
            skArc(sketch, "E31.trimOffspring", {"start": v(3.67, 1.59) * mm, "mid": v(3.65, 1.63) * mm, "end": v(3.64, 1.67) * mm});
            skArc(sketch, "E32.trimOffspring", {"start": v(3.73, 1.43) * mm, "mid": v(3.72, 1.47) * mm, "end": v(3.7, 1.51) * mm});
            skArc(sketch, "E33.trimOffspring", {"start": v(3.8, 1.27) * mm, "mid": v(3.78, 1.32) * mm, "end": v(3.76, 1.36) * mm});
            skArc(sketch, "E34.trimOffspring", {"start": v(3.84, 1.11) * mm, "mid": v(3.83, 1.16) * mm, "end": v(3.82, 1.2) * mm});
            skArc(sketch, "E35.trimOffspring", {"start": v(3.88, 0.95) * mm, "mid": v(3.87, 1) * mm, "end": v(3.86, 1.04) * mm});
            skArc(sketch, "E36.trimOffspring", {"start": v(3.92, 0.79) * mm, "mid": v(3.91, 0.83) * mm, "end": v(3.9, 0.87) * mm});
            skArc(sketch, "E37.trimOffspring", {"start": v(3.95, 0.62) * mm, "mid": v(3.94, 0.67) * mm, "end": v(3.94, 0.7) * mm});
            skArc(sketch, "E38.trimOffspring", {"start": v(3.97, 0.46) * mm, "mid": v(3.97, 0.5) * mm, "end": v(3.96, 0.54) * mm});
            skArc(sketch, "E39.trimOffspring", {"start": v(3.99, 0.3) * mm, "mid": v(3.99, 0.33) * mm, "end": v(3.98, 0.38) * mm});
            skArc(sketch, "E40.trimOffspring", {"start": v(4, 0.12) * mm, "mid": v(4, 0.17) * mm, "end": v(4, 0.21) * mm});
            skArc(sketch, "E41.trimOffspring", {"start": v(4, -0.04) * mm, "mid": v(4, 0) * mm, "end": v(4, 0.04) * mm});
            skArc(sketch, "E42.trimOffspring", {"start": v(4, -0.21) * mm, "mid": v(4, -0.17) * mm, "end": v(4, -0.12) * mm});
            skArc(sketch, "E43.trimOffspring", {"start": v(3.98, -0.38) * mm, "mid": v(3.99, -0.33) * mm, "end": v(3.99, -0.3) * mm});
            skArc(sketch, "E44.trimOffspring", {"start": v(3.96, -0.54) * mm, "mid": v(3.97, -0.5) * mm, "end": v(3.97, -0.46) * mm});
            skArc(sketch, "E45.trimOffspring", {"start": v(3.94, -0.71) * mm, "mid": v(3.94, -0.67) * mm, "end": v(3.95, -0.62) * mm});
            skArc(sketch, "E46.trimOffspring", {"start": v(3.9, -0.87) * mm, "mid": v(3.91, -0.83) * mm, "end": v(3.92, -0.79) * mm});
            skArc(sketch, "E47.trimOffspring", {"start": v(3.86, -1.04) * mm, "mid": v(3.87, -1) * mm, "end": v(3.88, -0.95) * mm});
            skArc(sketch, "E48.trimOffspring", {"start": v(3.82, -1.2) * mm, "mid": v(3.83, -1.16) * mm, "end": v(3.84, -1.11) * mm});
            skArc(sketch, "E49.trimOffspring", {"start": v(3.76, -1.36) * mm, "mid": v(3.78, -1.32) * mm, "end": v(3.8, -1.27) * mm});
            skArc(sketch, "E50.trimOffspring", {"start": v(3.7, -1.51) * mm, "mid": v(3.72, -1.47) * mm, "end": v(3.73, -1.43) * mm});
            skArc(sketch, "E51.trimOffspring", {"start": v(3.64, -1.67) * mm, "mid": v(3.65, -1.63) * mm, "end": v(3.67, -1.59) * mm});
            skArc(sketch, "E52.trimOffspring", {"start": v(3.56, -1.82) * mm, "mid": v(3.58, -1.78) * mm, "end": v(3.6, -1.74) * mm});
            skArc(sketch, "E53.trimOffspring", {"start": v(3.48, -1.97) * mm, "mid": v(3.5, -1.93) * mm, "end": v(3.53, -1.89) * mm});
            skArc(sketch, "E54.trimOffspring", {"start": v(3.4, -2.1) * mm, "mid": v(3.42, -2.07) * mm, "end": v(3.44, -2.04) * mm});
            skArc(sketch, "E55.trimOffspring", {"start": v(3.3, -2.25) * mm, "mid": v(3.33, -2.21) * mm, "end": v(3.36, -2.18) * mm});
            skArc(sketch, "E56.trimOffspring", {"start": v(3.21, -2.39) * mm, "mid": v(3.24, -2.35) * mm, "end": v(3.26, -2.32) * mm});
            skArc(sketch, "E57.trimOffspring", {"start": v(3.1, -2.52) * mm, "mid": v(3.13, -2.48) * mm, "end": v(3.16, -2.45) * mm});
            skArc(sketch, "E58.trimOffspring", {"start": v(3, -2.65) * mm, "mid": v(3.03, -2.61) * mm, "end": v(3.06, -2.58) * mm});
            skArc(sketch, "E59.trimOffspring", {"start": v(2.89, -2.77) * mm, "mid": v(2.92, -2.74) * mm, "end": v(2.95, -2.7) * mm});
            skArc(sketch, "E60.trimOffspring", {"start": v(2.77, -2.89) * mm, "mid": v(2.8, -2.86) * mm, "end": v(2.83, -2.83) * mm});
            skArc(sketch, "E61.trimOffspring", {"start": v(2.64, -3) * mm, "mid": v(2.68, -2.97) * mm, "end": v(2.7, -2.94) * mm});
            skArc(sketch, "E62.trimOffspring", {"start": v(2.52, -3.1) * mm, "mid": v(2.55, -3.08) * mm, "end": v(2.58, -3.05) * mm});
            skArc(sketch, "E63.trimOffspring", {"start": v(2.38, -3.21) * mm, "mid": v(2.42, -3.19) * mm, "end": v(2.45, -3.16) * mm});
            skArc(sketch, "E64.trimOffspring", {"start": v(2.25, -3.3) * mm, "mid": v(2.28, -3.28) * mm, "end": v(2.32, -3.26) * mm});
            skArc(sketch, "E65.trimOffspring", {"start": v(2.1, -3.4) * mm, "mid": v(2.14, -3.38) * mm, "end": v(2.18, -3.35) * mm});
            skArc(sketch, "E66.trimOffspring", {"start": v(1.96, -3.49) * mm, "mid": v(2, -3.46) * mm, "end": v(2.04, -3.44) * mm});
            skArc(sketch, "E67.trimOffspring", {"start": v(1.81, -3.56) * mm, "mid": v(1.85, -3.54) * mm, "end": v(1.9, -3.52) * mm});
            skArc(sketch, "E68.trimOffspring", {"start": v(1.66, -3.64) * mm, "mid": v(1.7, -3.62) * mm, "end": v(1.74, -3.6) * mm});
            skArc(sketch, "E69.trimOffspring", {"start": v(1.5, -3.7) * mm, "mid": v(1.55, -3.69) * mm, "end": v(1.59, -3.67) * mm});
            skArc(sketch, "E70.trimOffspring", {"start": v(1.35, -3.76) * mm, "mid": v(1.4, -3.75) * mm, "end": v(1.43, -3.73) * mm});
            skArc(sketch, "E71.trimOffspring", {"start": v(1.2, -3.82) * mm, "mid": v(1.24, -3.8) * mm, "end": v(1.28, -3.8) * mm});
            skArc(sketch, "E72.trimOffspring", {"start": v(1.03, -3.86) * mm, "mid": v(1.08, -3.85) * mm, "end": v(1.12, -3.84) * mm});
            skArc(sketch, "E73.trimOffspring", {"start": v(0.87, -3.9) * mm, "mid": v(0.91, -3.9) * mm, "end": v(0.96, -3.88) * mm});
            skArc(sketch, "E74.trimOffspring", {"start": v(0.7, -3.94) * mm, "mid": v(0.75, -3.93) * mm, "end": v(0.8, -3.92) * mm});
            skArc(sketch, "E75.trimOffspring", {"start": v(0.54, -3.96) * mm, "mid": v(0.58, -3.96) * mm, "end": v(0.63, -3.95) * mm});
            skArc(sketch, "E76.trimOffspring", {"start": v(0.37, -3.98) * mm, "mid": v(0.42, -3.98) * mm, "end": v(0.46, -3.97) * mm});
            skArc(sketch, "E77.trimOffspring", {"start": v(0.2, -4) * mm, "mid": v(0.25, -4) * mm, "end": v(0.3, -3.99) * mm});
            skArc(sketch, "E78.trimOffspring", {"start": v(0.04, -4) * mm, "mid": v(0.08, -4) * mm, "end": v(0.13, -4) * mm});
            skArc(sketch, "E79.trimOffspring", {"start": v(-0.13, -4) * mm, "mid": v(-0.08, -4) * mm, "end": v(-0.04, -4) * mm});
            skArc(sketch, "E80.trimOffspring", {"start": v(-0.3, -3.99) * mm, "mid": v(-0.25, -4) * mm, "end": v(-0.2, -4) * mm});
            skArc(sketch, "E81.trimOffspring", {"start": v(-0.46, -3.97) * mm, "mid": v(-0.42, -3.98) * mm, "end": v(-0.38, -3.98) * mm});
            skArc(sketch, "E82.trimOffspring", {"start": v(-0.63, -3.95) * mm, "mid": v(-0.58, -3.96) * mm, "end": v(-0.54, -3.96) * mm});
            skArc(sketch, "E83.trimOffspring", {"start": v(-0.8, -3.92) * mm, "mid": v(-0.75, -3.93) * mm, "end": v(-0.7, -3.94) * mm});
            skArc(sketch, "E84.trimOffspring", {"start": v(-0.96, -3.88) * mm, "mid": v(-0.91, -3.9) * mm, "end": v(-0.87, -3.9) * mm});
            skArc(sketch, "E85.trimOffspring", {"start": v(-1.12, -3.84) * mm, "mid": v(-1.08, -3.85) * mm, "end": v(-1.03, -3.86) * mm});
            skArc(sketch, "E86.trimOffspring", {"start": v(-1.28, -3.8) * mm, "mid": v(-1.24, -3.8) * mm, "end": v(-1.2, -3.82) * mm});
            skArc(sketch, "E87.trimOffspring", {"start": v(-1.44, -3.73) * mm, "mid": v(-1.4, -3.75) * mm, "end": v(-1.35, -3.76) * mm});
            skArc(sketch, "E88.trimOffspring", {"start": v(-1.6, -3.67) * mm, "mid": v(-1.55, -3.69) * mm, "end": v(-1.51, -3.7) * mm});
            skArc(sketch, "E89.trimOffspring", {"start": v(-1.74, -3.6) * mm, "mid": v(-1.7, -3.62) * mm, "end": v(-1.66, -3.64) * mm});
            skArc(sketch, "E90.trimOffspring", {"start": v(-1.9, -3.52) * mm, "mid": v(-1.85, -3.54) * mm, "end": v(-1.81, -3.56) * mm});
            skArc(sketch, "E91.trimOffspring", {"start": v(-2.04, -3.44) * mm, "mid": v(-2, -3.46) * mm, "end": v(-1.96, -3.49) * mm});
            skArc(sketch, "E92.trimOffspring", {"start": v(-2.18, -3.35) * mm, "mid": v(-2.14, -3.38) * mm, "end": v(-2.1, -3.4) * mm});
            skArc(sketch, "E93.trimOffspring", {"start": v(-2.32, -3.26) * mm, "mid": v(-2.28, -3.28) * mm, "end": v(-2.25, -3.3) * mm});
            skArc(sketch, "E94.trimOffspring", {"start": v(-2.45, -3.16) * mm, "mid": v(-2.42, -3.19) * mm, "end": v(-2.38, -3.21) * mm});
            skArc(sketch, "E95.trimOffspring", {"start": v(-2.58, -3.05) * mm, "mid": v(-2.55, -3.08) * mm, "end": v(-2.52, -3.1) * mm});
            skArc(sketch, "E96.trimOffspring", {"start": v(-2.7, -2.94) * mm, "mid": v(-2.68, -2.97) * mm, "end": v(-2.64, -3) * mm});
            skArc(sketch, "E97.trimOffspring", {"start": v(-2.83, -2.83) * mm, "mid": v(-2.8, -2.86) * mm, "end": v(-2.77, -2.89) * mm});
            skArc(sketch, "E98.trimOffspring", {"start": v(-2.95, -2.7) * mm, "mid": v(-2.92, -2.74) * mm, "end": v(-2.89, -2.77) * mm});
            skArc(sketch, "E99.trimOffspring", {"start": v(-3.06, -2.58) * mm, "mid": v(-3.03, -2.61) * mm, "end": v(-3, -2.65) * mm});
            skArc(sketch, "E100.trimOffspring", {"start": v(-3.16, -2.45) * mm, "mid": v(-3.13, -2.48) * mm, "end": v(-3.1, -2.52) * mm});
            skArc(sketch, "E101.trimOffspring", {"start": v(-3.26, -2.32) * mm, "mid": v(-3.24, -2.35) * mm, "end": v(-3.21, -2.39) * mm});
            skArc(sketch, "E102.trimOffspring", {"start": v(-3.36, -2.18) * mm, "mid": v(-3.33, -2.21) * mm, "end": v(-3.3, -2.25) * mm});
            skArc(sketch, "E103.trimOffspring", {"start": v(-3.44, -2.03) * mm, "mid": v(-3.42, -2.07) * mm, "end": v(-3.4, -2.1) * mm});
            skArc(sketch, "E104.trimOffspring", {"start": v(-3.53, -1.89) * mm, "mid": v(-3.5, -1.93) * mm, "end": v(-3.48, -1.96) * mm});
            skArc(sketch, "E105.trimOffspring", {"start": v(-3.6, -1.74) * mm, "mid": v(-3.58, -1.78) * mm, "end": v(-3.56, -1.82) * mm});
            skArc(sketch, "E106.trimOffspring", {"start": v(-3.67, -1.59) * mm, "mid": v(-3.65, -1.63) * mm, "end": v(-3.64, -1.67) * mm});
            skArc(sketch, "E107.trimOffspring", {"start": v(-3.73, -1.43) * mm, "mid": v(-3.72, -1.47) * mm, "end": v(-3.7, -1.51) * mm});
            skArc(sketch, "E108.trimOffspring", {"start": v(-3.8, -1.27) * mm, "mid": v(-3.78, -1.32) * mm, "end": v(-3.76, -1.36) * mm});
            skArc(sketch, "E109.trimOffspring", {"start": v(-3.84, -1.11) * mm, "mid": v(-3.83, -1.16) * mm, "end": v(-3.82, -1.2) * mm});
            skArc(sketch, "E110.trimOffspring", {"start": v(-3.88, -0.95) * mm, "mid": v(-3.87, -1) * mm, "end": v(-3.86, -1.04) * mm});
            skArc(sketch, "E111.trimOffspring", {"start": v(-3.92, -0.79) * mm, "mid": v(-3.91, -0.83) * mm, "end": v(-3.9, -0.87) * mm});
            skArc(sketch, "E112.trimOffspring", {"start": v(-3.95, -0.62) * mm, "mid": v(-3.94, -0.67) * mm, "end": v(-3.94, -0.7) * mm});
            skArc(sketch, "E113.trimOffspring", {"start": v(-3.97, -0.46) * mm, "mid": v(-3.97, -0.5) * mm, "end": v(-3.96, -0.54) * mm});
            skArc(sketch, "E114.trimOffspring", {"start": v(-3.99, -0.3) * mm, "mid": v(-3.99, -0.33) * mm, "end": v(-3.98, -0.38) * mm});
            skArc(sketch, "E115.trimOffspring", {"start": v(-4, -0.12) * mm, "mid": v(-4, -0.17) * mm, "end": v(-4, -0.21) * mm});
            skArc(sketch, "E116.trimOffspring", {"start": v(-4, 0.04) * mm, "mid": v(-4, 0) * mm, "end": v(-4, -0.04) * mm});
            skArc(sketch, "E117.trimOffspring", {"start": v(-4, 0.21) * mm, "mid": v(-4, 0.17) * mm, "end": v(-4, 0.12) * mm});
            skArc(sketch, "E118.trimOffspring", {"start": v(-3.98, 0.38) * mm, "mid": v(-3.99, 0.33) * mm, "end": v(-3.99, 0.3) * mm});
            skArc(sketch, "E119.trimOffspring", {"start": v(-3.96, 0.54) * mm, "mid": v(-3.97, 0.5) * mm, "end": v(-3.97, 0.46) * mm});
            skArc(sketch, "E120.trimOffspring", {"start": v(-3.94, 0.71) * mm, "mid": v(-3.94, 0.67) * mm, "end": v(-3.95, 0.62) * mm});
            skArc(sketch, "E121.trimOffspring", {"start": v(-3.9, 0.87) * mm, "mid": v(-3.91, 0.83) * mm, "end": v(-3.92, 0.79) * mm});
            skArc(sketch, "E122.trimOffspring", {"start": v(-3.86, 1.04) * mm, "mid": v(-3.87, 1) * mm, "end": v(-3.88, 0.95) * mm});
            skArc(sketch, "E123.trimOffspring", {"start": v(-3.82, 1.2) * mm, "mid": v(-3.83, 1.16) * mm, "end": v(-3.84, 1.11) * mm});
            skArc(sketch, "E124.trimOffspring", {"start": v(-3.76, 1.36) * mm, "mid": v(-3.78, 1.32) * mm, "end": v(-3.8, 1.27) * mm});
            skArc(sketch, "E125.trimOffspring", {"start": v(-3.7, 1.51) * mm, "mid": v(-3.72, 1.47) * mm, "end": v(-3.73, 1.43) * mm});
            skArc(sketch, "E126.trimOffspring", {"start": v(-3.64, 1.67) * mm, "mid": v(-3.65, 1.63) * mm, "end": v(-3.67, 1.59) * mm});
            skArc(sketch, "E127.trimOffspring", {"start": v(-3.56, 1.82) * mm, "mid": v(-3.58, 1.78) * mm, "end": v(-3.6, 1.74) * mm});
            skArc(sketch, "E128.trimOffspring", {"start": v(-3.48, 1.97) * mm, "mid": v(-3.5, 1.93) * mm, "end": v(-3.53, 1.89) * mm});
            skArc(sketch, "E129.trimOffspring", {"start": v(-3.4, 2.1) * mm, "mid": v(-3.42, 2.07) * mm, "end": v(-3.44, 2.04) * mm});
            skArc(sketch, "E130.trimOffspring", {"start": v(-3.3, 2.25) * mm, "mid": v(-3.33, 2.21) * mm, "end": v(-3.36, 2.18) * mm});
            skArc(sketch, "E131.trimOffspring", {"start": v(-3.21, 2.39) * mm, "mid": v(-3.24, 2.35) * mm, "end": v(-3.26, 2.32) * mm});
            skArc(sketch, "E132.trimOffspring", {"start": v(-3.1, 2.52) * mm, "mid": v(-3.13, 2.48) * mm, "end": v(-3.16, 2.45) * mm});
            skArc(sketch, "E133.trimOffspring", {"start": v(-3, 2.65) * mm, "mid": v(-3.03, 2.61) * mm, "end": v(-3.06, 2.58) * mm});
            skArc(sketch, "E134.trimOffspring", {"start": v(-2.89, 2.77) * mm, "mid": v(-2.92, 2.74) * mm, "end": v(-2.95, 2.7) * mm});
            skArc(sketch, "E135.trimOffspring", {"start": v(-2.77, 2.89) * mm, "mid": v(-2.8, 2.86) * mm, "end": v(-2.83, 2.83) * mm});
            skArc(sketch, "E136.trimOffspring", {"start": v(-2.64, 3) * mm, "mid": v(-2.68, 2.97) * mm, "end": v(-2.7, 2.94) * mm});
            skArc(sketch, "E137.trimOffspring", {"start": v(-2.52, 3.1) * mm, "mid": v(-2.55, 3.08) * mm, "end": v(-2.58, 3.05) * mm});
            skArc(sketch, "E138.trimOffspring", {"start": v(-2.38, 3.21) * mm, "mid": v(-2.42, 3.19) * mm, "end": v(-2.45, 3.16) * mm});
            skArc(sketch, "E139.trimOffspring", {"start": v(-2.25, 3.3) * mm, "mid": v(-2.28, 3.28) * mm, "end": v(-2.32, 3.26) * mm});
            skArc(sketch, "E140.trimOffspring", {"start": v(-2.1, 3.4) * mm, "mid": v(-2.14, 3.38) * mm, "end": v(-2.18, 3.35) * mm});
            skArc(sketch, "E141.trimOffspring", {"start": v(-1.96, 3.49) * mm, "mid": v(-2, 3.46) * mm, "end": v(-2.04, 3.44) * mm});
            skArc(sketch, "E142.trimOffspring", {"start": v(-1.81, 3.56) * mm, "mid": v(-1.85, 3.54) * mm, "end": v(-1.9, 3.52) * mm});
            skArc(sketch, "E143.trimOffspring", {"start": v(-1.66, 3.64) * mm, "mid": v(-1.7, 3.62) * mm, "end": v(-1.74, 3.6) * mm});
            skArc(sketch, "E144.trimOffspring", {"start": v(-1.5, 3.7) * mm, "mid": v(-1.55, 3.69) * mm, "end": v(-1.59, 3.67) * mm});
            skArc(sketch, "E145.trimOffspring", {"start": v(-1.35, 3.76) * mm, "mid": v(-1.4, 3.75) * mm, "end": v(-1.43, 3.73) * mm});
            skArc(sketch, "E146.trimOffspring", {"start": v(-1.2, 3.82) * mm, "mid": v(-1.24, 3.8) * mm, "end": v(-1.28, 3.8) * mm});
            skArc(sketch, "E147.trimOffspring", {"start": v(-0.2, 4) * mm, "mid": v(-0.25, 4) * mm, "end": v(-0.3, 3.99) * mm});
            skArc(sketch, "E148.trimOffspring", {"start": v(-0.37, 3.98) * mm, "mid": v(-0.42, 3.98) * mm, "end": v(-0.46, 3.97) * mm});
            skArc(sketch, "E149.trimOffspring", {"start": v(-0.54, 3.96) * mm, "mid": v(-0.58, 3.96) * mm, "end": v(-0.63, 3.95) * mm});
            skArc(sketch, "E150.trimOffspring", {"start": v(-0.7, 3.94) * mm, "mid": v(-0.75, 3.93) * mm, "end": v(-0.8, 3.92) * mm});
            skArc(sketch, "E151.trimOffspring", {"start": v(-0.87, 3.9) * mm, "mid": v(-0.91, 3.9) * mm, "end": v(-0.96, 3.88) * mm});
            skArc(sketch, "E152.trimOffspring", {"start": v(-1.03, 3.86) * mm, "mid": v(-1.08, 3.85) * mm, "end": v(-1.12, 3.84) * mm});
            skSolve(sketch);
        }
        {
            var Q0;
            Q0=makeQuery(id+"F0.imprint","IMPRINT",FACE,{"disambiguationData":[TD([[makeQuery(id+"F0.imprint","IMPRINT",EDGE,{"derivedFrom":sQuery(id+"F0.wireOp",EDGE,"E0")}),1.0]])]});
            extrude(context, id + "F1", {"entities" : qUnion([Q0]), "depth" : 10 * mm});
        }
        {
            var Q0;
            Q0=makeQuery(id+"F1.opExtrude","CAP_FACE",FACE,{"disambiguationData":[OSD([sQuery(id+"F0.wireOp",EDGE,"E0"),sQuery(id+"F0.wireOp",EDGE,"E1"),sQuery(id+"F0.wireOp",EDGE,"E2"),sQuery(id+"F0.wireOp",EDGE,"E3.1.0"),sQuery(id+"F0.wireOp",EDGE,"E3.1.1"),sQuery(id+"F0.wireOp",EDGE,"E3.2.0"),sQuery(id+"F0.wireOp",EDGE,"E3.2.1"),sQuery(id+"F0.wireOp",EDGE,"E3.3.0"),sQuery(id+"F0.wireOp",EDGE,"E3.3.1"),sQuery(id+"F0.wireOp",EDGE,"E3.4.0"),sQuery(id+"F0.wireOp",EDGE,"E3.4.1"),sQuery(id+"F0.wireOp",EDGE,"E3.5.0"),sQuery(id+"F0.wireOp",EDGE,"E3.5.1"),sQuery(id+"F0.wireOp",EDGE,"E3.6.0"),sQuery(id+"F0.wireOp",EDGE,"E3.6.1"),sQuery(id+"F0.wireOp",EDGE,"E3.7.0"),sQuery(id+"F0.wireOp",EDGE,"E3.7.1"),sQuery(id+"F0.wireOp",EDGE,"E3.8.0"),sQuery(id+"F0.wireOp",EDGE,"E3.8.1"),sQuery(id+"F0.wireOp",EDGE,"E3.9.0"),sQuery(id+"F0.wireOp",EDGE,"E3.9.1"),sQuery(id+"F0.wireOp",EDGE,"E3.10.0"),sQuery(id+"F0.wireOp",EDGE,"E3.10.1"),sQuery(id+"F0.wireOp",EDGE,"E3.11.0"),sQuery(id+"F0.wireOp",EDGE,"E3.11.1"),sQuery(id+"F0.wireOp",EDGE,"E3.12.0"),sQuery(id+"F0.wireOp",EDGE,"E3.12.1"),sQuery(id+"F0.wireOp",EDGE,"E3.13.0"),sQuery(id+"F0.wireOp",EDGE,"E3.13.1"),sQuery(id+"F0.wireOp",EDGE,"E3.14.0"),sQuery(id+"F0.wireOp",EDGE,"E3.14.1"),sQuery(id+"F0.wireOp",EDGE,"E3.15.0"),sQuery(id+"F0.wireOp",EDGE,"E3.15.1"),sQuery(id+"F0.wireOp",EDGE,"E3.16.0"),sQuery(id+"F0.wireOp",EDGE,"E3.16.1"),sQuery(id+"F0.wireOp",EDGE,"E3.17.0"),sQuery(id+"F0.wireOp",EDGE,"E3.17.1"),sQuery(id+"F0.wireOp",EDGE,"E3.18.0"),sQuery(id+"F0.wireOp",EDGE,"E3.18.1"),sQuery(id+"F0.wireOp",EDGE,"E3.19.0"),sQuery(id+"F0.wireOp",EDGE,"E3.19.1"),sQuery(id+"F0.wireOp",EDGE,"E3.20.0"),sQuery(id+"F0.wireOp",EDGE,"E3.20.1"),sQuery(id+"F0.wireOp",EDGE,"E3.21.0"),sQuery(id+"F0.wireOp",EDGE,"E3.21.1"),sQuery(id+"F0.wireOp",EDGE,"E3.22.0"),sQuery(id+"F0.wireOp",EDGE,"E3.22.1"),sQuery(id+"F0.wireOp",EDGE,"E3.23.0"),sQuery(id+"F0.wireOp",EDGE,"E3.23.1"),sQuery(id+"F0.wireOp",EDGE,"E3.24.0"),sQuery(id+"F0.wireOp",EDGE,"E3.24.1"),sQuery(id+"F0.wireOp",EDGE,"E3.25.0"),sQuery(id+"F0.wireOp",EDGE,"E3.25.1"),sQuery(id+"F0.wireOp",EDGE,"E3.26.0"),sQuery(id+"F0.wireOp",EDGE,"E3.26.1"),sQuery(id+"F0.wireOp",EDGE,"E3.27.0"),sQuery(id+"F0.wireOp",EDGE,"E3.27.1"),sQuery(id+"F0.wireOp",EDGE,"E3.28.0"),sQuery(id+"F0.wireOp",EDGE,"E3.28.1"),sQuery(id+"F0.wireOp",EDGE,"E3.29.0"),sQuery(id+"F0.wireOp",EDGE,"E3.29.1"),sQuery(id+"F0.wireOp",EDGE,"E3.30.0"),sQuery(id+"F0.wireOp",EDGE,"E3.30.1"),sQuery(id+"F0.wireOp",EDGE,"E3.31.0"),sQuery(id+"F0.wireOp",EDGE,"E3.31.1"),sQuery(id+"F0.wireOp",EDGE,"E3.32.0"),sQuery(id+"F0.wireOp",EDGE,"E3.32.1"),sQuery(id+"F0.wireOp",EDGE,"E3.33.0"),sQuery(id+"F0.wireOp",EDGE,"E3.33.1"),sQuery(id+"F0.wireOp",EDGE,"E3.34.0"),sQuery(id+"F0.wireOp",EDGE,"E3.34.1"),sQuery(id+"F0.wireOp",EDGE,"E3.35.0"),sQuery(id+"F0.wireOp",EDGE,"E3.35.1"),sQuery(id+"F0.wireOp",EDGE,"E3.36.0"),sQuery(id+"F0.wireOp",EDGE,"E3.36.1"),sQuery(id+"F0.wireOp",EDGE,"E3.37.0"),sQuery(id+"F0.wireOp",EDGE,"E3.37.1"),sQuery(id+"F0.wireOp",EDGE,"E3.38.0"),sQuery(id+"F0.wireOp",EDGE,"E3.38.1"),sQuery(id+"F0.wireOp",EDGE,"E3.39.0"),sQuery(id+"F0.wireOp",EDGE,"E3.39.1"),sQuery(id+"F0.wireOp",EDGE,"E3.40.0"),sQuery(id+"F0.wireOp",EDGE,"E3.40.1"),sQuery(id+"F0.wireOp",EDGE,"E3.41.0"),sQuery(id+"F0.wireOp",EDGE,"E3.41.1"),sQuery(id+"F0.wireOp",EDGE,"E3.42.0"),sQuery(id+"F0.wireOp",EDGE,"E3.42.1"),sQuery(id+"F0.wireOp",EDGE,"E3.43.0"),sQuery(id+"F0.wireOp",EDGE,"E3.43.1"),sQuery(id+"F0.wireOp",EDGE,"E3.44.0"),sQuery(id+"F0.wireOp",EDGE,"E3.44.1"),sQuery(id+"F0.wireOp",EDGE,"E3.45.0"),sQuery(id+"F0.wireOp",EDGE,"E3.45.1"),sQuery(id+"F0.wireOp",EDGE,"E3.46.0"),sQuery(id+"F0.wireOp",EDGE,"E3.46.1"),sQuery(id+"F0.wireOp",EDGE,"E3.47.0"),sQuery(id+"F0.wireOp",EDGE,"E3.47.1"),sQuery(id+"F0.wireOp",EDGE,"E3.48.0"),sQuery(id+"F0.wireOp",EDGE,"E3.48.1"),sQuery(id+"F0.wireOp",EDGE,"E3.49.0"),sQuery(id+"F0.wireOp",EDGE,"E3.49.1"),sQuery(id+"F0.wireOp",EDGE,"E3.50.0"),sQuery(id+"F0.wireOp",EDGE,"E3.50.1"),sQuery(id+"F0.wireOp",EDGE,"E3.51.0"),sQuery(id+"F0.wireOp",EDGE,"E3.51.1"),sQuery(id+"F0.wireOp",EDGE,"E3.52.0"),sQuery(id+"F0.wireOp",EDGE,"E3.52.1"),sQuery(id+"F0.wireOp",EDGE,"E3.53.0"),sQuery(id+"F0.wireOp",EDGE,"E3.53.1"),sQuery(id+"F0.wireOp",EDGE,"E3.54.0"),sQuery(id+"F0.wireOp",EDGE,"E3.54.1"),sQuery(id+"F0.wireOp",EDGE,"E3.55.0"),sQuery(id+"F0.wireOp",EDGE,"E3.55.1"),sQuery(id+"F0.wireOp",EDGE,"E3.56.0"),sQuery(id+"F0.wireOp",EDGE,"E3.56.1"),sQuery(id+"F0.wireOp",EDGE,"E3.57.0"),sQuery(id+"F0.wireOp",EDGE,"E3.57.1"),sQuery(id+"F0.wireOp",EDGE,"E3.58.0"),sQuery(id+"F0.wireOp",EDGE,"E3.58.1"),sQuery(id+"F0.wireOp",EDGE,"E3.59.0"),sQuery(id+"F0.wireOp",EDGE,"E3.59.1"),sQuery(id+"F0.wireOp",EDGE,"E3.60.0"),sQuery(id+"F0.wireOp",EDGE,"E3.60.1"),sQuery(id+"F0.wireOp",EDGE,"E3.61.0"),sQuery(id+"F0.wireOp",EDGE,"E3.61.1"),sQuery(id+"F0.wireOp",EDGE,"E3.62.0"),sQuery(id+"F0.wireOp",EDGE,"E3.62.1"),sQuery(id+"F0.wireOp",EDGE,"E3.63.0"),sQuery(id+"F0.wireOp",EDGE,"E3.63.1"),sQuery(id+"F0.wireOp",EDGE,"E3.64.0"),sQuery(id+"F0.wireOp",EDGE,"E3.64.1"),sQuery(id+"F0.wireOp",EDGE,"E3.65.0"),sQuery(id+"F0.wireOp",EDGE,"E3.65.1"),sQuery(id+"F0.wireOp",EDGE,"E3.66.0"),sQuery(id+"F0.wireOp",EDGE,"E3.66.1"),sQuery(id+"F0.wireOp",EDGE,"E3.67.0"),sQuery(id+"F0.wireOp",EDGE,"E3.67.1"),sQuery(id+"F0.wireOp",EDGE,"E3.68.0"),sQuery(id+"F0.wireOp",EDGE,"E3.68.1"),sQuery(id+"F0.wireOp",EDGE,"E3.69.0"),sQuery(id+"F0.wireOp",EDGE,"E3.69.1"),sQuery(id+"F0.wireOp",EDGE,"E3.70.0"),sQuery(id+"F0.wireOp",EDGE,"E3.70.1"),sQuery(id+"F0.wireOp",EDGE,"E3.71.0"),sQuery(id+"F0.wireOp",EDGE,"E3.71.1"),sQuery(id+"F0.wireOp",EDGE,"E3.72.0"),sQuery(id+"F0.wireOp",EDGE,"E3.72.1"),sQuery(id+"F0.wireOp",EDGE,"E3.73.0"),sQuery(id+"F0.wireOp",EDGE,"E3.73.1"),sQuery(id+"F0.wireOp",EDGE,"E3.74.0"),sQuery(id+"F0.wireOp",EDGE,"E3.74.1"),sQuery(id+"F0.wireOp",EDGE,"E3.75.0"),sQuery(id+"F0.wireOp",EDGE,"E3.75.1"),sQuery(id+"F0.wireOp",EDGE,"E3.76.0"),sQuery(id+"F0.wireOp",EDGE,"E3.76.1"),sQuery(id+"F0.wireOp",EDGE,"E3.77.0"),sQuery(id+"F0.wireOp",EDGE,"E3.77.1"),sQuery(id+"F0.wireOp",EDGE,"E3.78.0"),sQuery(id+"F0.wireOp",EDGE,"E3.78.1"),sQuery(id+"F0.wireOp",EDGE,"E3.79.0"),sQuery(id+"F0.wireOp",EDGE,"E3.79.1"),sQuery(id+"F0.wireOp",EDGE,"E3.80.0"),sQuery(id+"F0.wireOp",EDGE,"E3.80.1"),sQuery(id+"F0.wireOp",EDGE,"E3.81.0"),sQuery(id+"F0.wireOp",EDGE,"E3.81.1"),sQuery(id+"F0.wireOp",EDGE,"E3.82.0"),sQuery(id+"F0.wireOp",EDGE,"E3.82.1"),sQuery(id+"F0.wireOp",EDGE,"E3.83.0"),sQuery(id+"F0.wireOp",EDGE,"E3.83.1"),sQuery(id+"F0.wireOp",EDGE,"E3.84.0"),sQuery(id+"F0.wireOp",EDGE,"E3.84.1"),sQuery(id+"F0.wireOp",EDGE,"E3.85.0"),sQuery(id+"F0.wireOp",EDGE,"E3.85.1"),sQuery(id+"F0.wireOp",EDGE,"E3.86.0"),sQuery(id+"F0.wireOp",EDGE,"E3.86.1"),sQuery(id+"F0.wireOp",EDGE,"E3.87.0"),sQuery(id+"F0.wireOp",EDGE,"E3.87.1"),sQuery(id+"F0.wireOp",EDGE,"E3.88.0"),sQuery(id+"F0.wireOp",EDGE,"E3.88.1"),sQuery(id+"F0.wireOp",EDGE,"E3.89.0"),sQuery(id+"F0.wireOp",EDGE,"E3.89.1"),sQuery(id+"F0.wireOp",EDGE,"E3.90.0"),sQuery(id+"F0.wireOp",EDGE,"E3.90.1"),sQuery(id+"F0.wireOp",EDGE,"E3.91.0"),sQuery(id+"F0.wireOp",EDGE,"E3.91.1"),sQuery(id+"F0.wireOp",EDGE,"E3.92.0"),sQuery(id+"F0.wireOp",EDGE,"E3.92.1"),sQuery(id+"F0.wireOp",EDGE,"E3.93.0"),sQuery(id+"F0.wireOp",EDGE,"E3.93.1"),sQuery(id+"F0.wireOp",EDGE,"E3.94.0"),sQuery(id+"F0.wireOp",EDGE,"E3.94.1"),sQuery(id+"F0.wireOp",EDGE,"E3.95.0"),sQuery(id+"F0.wireOp",EDGE,"E3.95.1"),sQuery(id+"F0.wireOp",EDGE,"E3.96.0"),sQuery(id+"F0.wireOp",EDGE,"E3.96.1"),sQuery(id+"F0.wireOp",EDGE,"E3.97.0"),sQuery(id+"F0.wireOp",EDGE,"E3.97.1"),sQuery(id+"F0.wireOp",EDGE,"E3.98.0"),sQuery(id+"F0.wireOp",EDGE,"E3.98.1"),sQuery(id+"F0.wireOp",EDGE,"E3.99.0"),sQuery(id+"F0.wireOp",EDGE,"E3.99.1"),sQuery(id+"F0.wireOp",EDGE,"E3.100.0"),sQuery(id+"F0.wireOp",EDGE,"E3.100.1"),sQuery(id+"F0.wireOp",EDGE,"E3.101.0"),sQuery(id+"F0.wireOp",EDGE,"E3.101.1"),sQuery(id+"F0.wireOp",EDGE,"E3.102.0"),sQuery(id+"F0.wireOp",EDGE,"E3.102.1"),sQuery(id+"F0.wireOp",EDGE,"E3.103.0"),sQuery(id+"F0.wireOp",EDGE,"E3.103.1"),sQuery(id+"F0.wireOp",EDGE,"E3.104.0"),sQuery(id+"F0.wireOp",EDGE,"E3.104.1"),sQuery(id+"F0.wireOp",EDGE,"E3.105.0"),sQuery(id+"F0.wireOp",EDGE,"E3.105.1"),sQuery(id+"F0.wireOp",EDGE,"E3.106.0"),sQuery(id+"F0.wireOp",EDGE,"E3.106.1"),sQuery(id+"F0.wireOp",EDGE,"E3.107.0"),sQuery(id+"F0.wireOp",EDGE,"E3.107.1"),sQuery(id+"F0.wireOp",EDGE,"E3.108.0"),sQuery(id+"F0.wireOp",EDGE,"E3.108.1"),sQuery(id+"F0.wireOp",EDGE,"E3.109.0"),sQuery(id+"F0.wireOp",EDGE,"E3.109.1"),sQuery(id+"F0.wireOp",EDGE,"E3.110.0"),sQuery(id+"F0.wireOp",EDGE,"E3.110.1"),sQuery(id+"F0.wireOp",EDGE,"E3.111.0"),sQuery(id+"F0.wireOp",EDGE,"E3.111.1"),sQuery(id+"F0.wireOp",EDGE,"E3.112.0"),sQuery(id+"F0.wireOp",EDGE,"E3.112.1"),sQuery(id+"F0.wireOp",EDGE,"E3.113.0"),sQuery(id+"F0.wireOp",EDGE,"E3.113.1"),sQuery(id+"F0.wireOp",EDGE,"E3.114.0"),sQuery(id+"F0.wireOp",EDGE,"E3.114.1"),sQuery(id+"F0.wireOp",EDGE,"E3.115.0"),sQuery(id+"F0.wireOp",EDGE,"E3.115.1"),sQuery(id+"F0.wireOp",EDGE,"E3.116.0"),sQuery(id+"F0.wireOp",EDGE,"E3.116.1"),sQuery(id+"F0.wireOp",EDGE,"E3.117.0"),sQuery(id+"F0.wireOp",EDGE,"E3.117.1"),sQuery(id+"F0.wireOp",EDGE,"E3.118.0"),sQuery(id+"F0.wireOp",EDGE,"E3.118.1"),sQuery(id+"F0.wireOp",EDGE,"E3.119.0"),sQuery(id+"F0.wireOp",EDGE,"E3.119.1"),sQuery(id+"F0.wireOp",EDGE,"E3.120.0"),sQuery(id+"F0.wireOp",EDGE,"E3.120.1"),sQuery(id+"F0.wireOp",EDGE,"E3.121.0"),sQuery(id+"F0.wireOp",EDGE,"E3.121.1"),sQuery(id+"F0.wireOp",EDGE,"E3.122.0"),sQuery(id+"F0.wireOp",EDGE,"E3.122.1"),sQuery(id+"F0.wireOp",EDGE,"E3.123.0"),sQuery(id+"F0.wireOp",EDGE,"E3.123.1"),sQuery(id+"F0.wireOp",EDGE,"E3.124.0"),sQuery(id+"F0.wireOp",EDGE,"E3.124.1"),sQuery(id+"F0.wireOp",EDGE,"E3.125.0"),sQuery(id+"F0.wireOp",EDGE,"E3.125.1"),sQuery(id+"F0.wireOp",EDGE,"E3.126.0"),sQuery(id+"F0.wireOp",EDGE,"E3.126.1"),sQuery(id+"F0.wireOp",EDGE,"E3.127.0"),sQuery(id+"F0.wireOp",EDGE,"E3.127.1"),sQuery(id+"F0.wireOp",EDGE,"E3.128.0"),sQuery(id+"F0.wireOp",EDGE,"E3.128.1"),sQuery(id+"F0.wireOp",EDGE,"E3.129.0"),sQuery(id+"F0.wireOp",EDGE,"E3.129.1"),sQuery(id+"F0.wireOp",EDGE,"E3.130.0"),sQuery(id+"F0.wireOp",EDGE,"E3.130.1"),sQuery(id+"F0.wireOp",EDGE,"E3.131.0"),sQuery(id+"F0.wireOp",EDGE,"E3.131.1"),sQuery(id+"F0.wireOp",EDGE,"E3.132.0"),sQuery(id+"F0.wireOp",EDGE,"E3.132.1"),sQuery(id+"F0.wireOp",EDGE,"E3.133.0"),sQuery(id+"F0.wireOp",EDGE,"E3.133.1"),sQuery(id+"F0.wireOp",EDGE,"E3.134.0"),sQuery(id+"F0.wireOp",EDGE,"E3.134.1"),sQuery(id+"F0.wireOp",EDGE,"E3.135.0"),sQuery(id+"F0.wireOp",EDGE,"E3.135.1"),sQuery(id+"F0.wireOp",EDGE,"E3.136.0"),sQuery(id+"F0.wireOp",EDGE,"E3.136.1"),sQuery(id+"F0.wireOp",EDGE,"E3.137.0"),sQuery(id+"F0.wireOp",EDGE,"E3.137.1"),sQuery(id+"F0.wireOp",EDGE,"E3.138.0"),sQuery(id+"F0.wireOp",EDGE,"E3.138.1"),sQuery(id+"F0.wireOp",EDGE,"E3.139.0"),sQuery(id+"F0.wireOp",EDGE,"E3.139.1"),sQuery(id+"F0.wireOp",EDGE,"E3.140.0"),sQuery(id+"F0.wireOp",EDGE,"E3.140.1"),sQuery(id+"F0.wireOp",EDGE,"E3.141.0"),sQuery(id+"F0.wireOp",EDGE,"E3.141.1"),sQuery(id+"F0.wireOp",EDGE,"E3.142.0"),sQuery(id+"F0.wireOp",EDGE,"E3.142.1"),sQuery(id+"F0.wireOp",EDGE,"E3.143.0"),sQuery(id+"F0.wireOp",EDGE,"E3.143.1"),sQuery(id+"F0.wireOp",EDGE,"E3.144.0"),sQuery(id+"F0.wireOp",EDGE,"E3.144.1"),sQuery(id+"F0.wireOp",EDGE,"E3.145.0"),sQuery(id+"F0.wireOp",EDGE,"E3.145.1"),sQuery(id+"F0.wireOp",EDGE,"E3.146.0"),sQuery(id+"F0.wireOp",EDGE,"E3.146.1"),sQuery(id+"F0.wireOp",EDGE,"E3.147.0"),sQuery(id+"F0.wireOp",EDGE,"E3.147.1"),sQuery(id+"F0.wireOp",EDGE,"E3.148.0"),sQuery(id+"F0.wireOp",EDGE,"E3.148.1"),sQuery(id+"F0.wireOp",EDGE,"E3.149.0"),sQuery(id+"F0.wireOp",EDGE,"E3.149.1"),sQuery(id+"F0.wireOp",EDGE,"E4.trimOffspring"),sQuery(id+"F0.wireOp",EDGE,"E5.trimOffspring"),sQuery(id+"F0.wireOp",EDGE,"E6.trimOffspring"),sQuery(id+"F0.wireOp",EDGE,"E7.trimOffspring"),sQuery(id+"F0.wireOp",EDGE,"E8.trimOffspring"),sQuery(id+"F0.wireOp",EDGE,"E9.trimOffspring"),sQuery(id+"F0.wireOp",EDGE,"E10.trimOffspring"),sQuery(id+"F0.wireOp",EDGE,"E11.trimOffspring"),sQuery(id+"F0.wireOp",EDGE,"E12.trimOffspring"),sQuery(id+"F0.wireOp",EDGE,"E13.trimOffspring"),sQuery(id+"F0.wireOp",EDGE,"E14.trimOffspring"),sQuery(id+"F0.wireOp",EDGE,"E15.trimOffspring"),sQuery(id+"F0.wireOp",EDGE,"E16.trimOffspring"),sQuery(id+"F0.wireOp",EDGE,"E17.trimOffspring"),sQuery(id+"F0.wireOp",EDGE,"E18.trimOffspring"),sQuery(id+"F0.wireOp",EDGE,"E19.trimOffspring"),sQuery(id+"F0.wireOp",EDGE,"E20.trimOffspring"),sQuery(id+"F0.wireOp",EDGE,"E21.trimOffspring"),sQuery(id+"F0.wireOp",EDGE,"E22.trimOffspring"),sQuery(id+"F0.wireOp",EDGE,"E23.trimOffspring"),sQuery(id+"F0.wireOp",EDGE,"E24.trimOffspring"),sQuery(id+"F0.wireOp",EDGE,"E25.trimOffspring"),sQuery(id+"F0.wireOp",EDGE,"E26.trimOffspring"),sQuery(id+"F0.wireOp",EDGE,"E27.trimOffspring"),sQuery(id+"F0.wireOp",EDGE,"E28.trimOffspring"),sQuery(id+"F0.wireOp",EDGE,"E29.trimOffspring"),sQuery(id+"F0.wireOp",EDGE,"E30.trimOffspring"),sQuery(id+"F0.wireOp",EDGE,"E31.trimOffspring"),sQuery(id+"F0.wireOp",EDGE,"E32.trimOffspring"),sQuery(id+"F0.wireOp",EDGE,"E33.trimOffspring"),sQuery(id+"F0.wireOp",EDGE,"E34.trimOffspring"),sQuery(id+"F0.wireOp",EDGE,"E35.trimOffspring"),sQuery(id+"F0.wireOp",EDGE,"E36.trimOffspring"),sQuery(id+"F0.wireOp",EDGE,"E37.trimOffspring"),sQuery(id+"F0.wireOp",EDGE,"E38.trimOffspring"),sQuery(id+"F0.wireOp",EDGE,"E39.trimOffspring"),sQuery(id+"F0.wireOp",EDGE,"E40.trimOffspring"),sQuery(id+"F0.wireOp",EDGE,"E41.trimOffspring"),sQuery(id+"F0.wireOp",EDGE,"E42.trimOffspring"),sQuery(id+"F0.wireOp",EDGE,"E43.trimOffspring"),sQuery(id+"F0.wireOp",EDGE,"E44.trimOffspring"),sQuery(id+"F0.wireOp",EDGE,"E45.trimOffspring"),sQuery(id+"F0.wireOp",EDGE,"E46.trimOffspring"),sQuery(id+"F0.wireOp",EDGE,"E47.trimOffspring"),sQuery(id+"F0.wireOp",EDGE,"E48.trimOffspring"),sQuery(id+"F0.wireOp",EDGE,"E49.trimOffspring"),sQuery(id+"F0.wireOp",EDGE,"E50.trimOffspring"),sQuery(id+"F0.wireOp",EDGE,"E51.trimOffspring"),sQuery(id+"F0.wireOp",EDGE,"E52.trimOffspring"),sQuery(id+"F0.wireOp",EDGE,"E53.trimOffspring"),sQuery(id+"F0.wireOp",EDGE,"E54.trimOffspring"),sQuery(id+"F0.wireOp",EDGE,"E55.trimOffspring"),sQuery(id+"F0.wireOp",EDGE,"E56.trimOffspring"),sQuery(id+"F0.wireOp",EDGE,"E57.trimOffspring"),sQuery(id+"F0.wireOp",EDGE,"E58.trimOffspring"),sQuery(id+"F0.wireOp",EDGE,"E59.trimOffspring"),sQuery(id+"F0.wireOp",EDGE,"E60.trimOffspring"),sQuery(id+"F0.wireOp",EDGE,"E61.trimOffspring"),sQuery(id+"F0.wireOp",EDGE,"E62.trimOffspring"),sQuery(id+"F0.wireOp",EDGE,"E63.trimOffspring"),sQuery(id+"F0.wireOp",EDGE,"E64.trimOffspring"),sQuery(id+"F0.wireOp",EDGE,"E65.trimOffspring"),sQuery(id+"F0.wireOp",EDGE,"E66.trimOffspring"),sQuery(id+"F0.wireOp",EDGE,"E67.trimOffspring"),sQuery(id+"F0.wireOp",EDGE,"E68.trimOffspring"),sQuery(id+"F0.wireOp",EDGE,"E69.trimOffspring"),sQuery(id+"F0.wireOp",EDGE,"E70.trimOffspring"),sQuery(id+"F0.wireOp",EDGE,"E71.trimOffspring"),sQuery(id+"F0.wireOp",EDGE,"E72.trimOffspring"),sQuery(id+"F0.wireOp",EDGE,"E73.trimOffspring"),sQuery(id+"F0.wireOp",EDGE,"E74.trimOffspring"),sQuery(id+"F0.wireOp",EDGE,"E75.trimOffspring"),sQuery(id+"F0.wireOp",EDGE,"E76.trimOffspring"),sQuery(id+"F0.wireOp",EDGE,"E77.trimOffspring"),sQuery(id+"F0.wireOp",EDGE,"E78.trimOffspring"),sQuery(id+"F0.wireOp",EDGE,"E79.trimOffspring"),sQuery(id+"F0.wireOp",EDGE,"E80.trimOffspring"),sQuery(id+"F0.wireOp",EDGE,"E81.trimOffspring"),sQuery(id+"F0.wireOp",EDGE,"E82.trimOffspring"),sQuery(id+"F0.wireOp",EDGE,"E83.trimOffspring"),sQuery(id+"F0.wireOp",EDGE,"E84.trimOffspring"),sQuery(id+"F0.wireOp",EDGE,"E85.trimOffspring"),sQuery(id+"F0.wireOp",EDGE,"E86.trimOffspring"),sQuery(id+"F0.wireOp",EDGE,"E87.trimOffspring"),sQuery(id+"F0.wireOp",EDGE,"E88.trimOffspring"),sQuery(id+"F0.wireOp",EDGE,"E89.trimOffspring"),sQuery(id+"F0.wireOp",EDGE,"E90.trimOffspring"),sQuery(id+"F0.wireOp",EDGE,"E91.trimOffspring"),sQuery(id+"F0.wireOp",EDGE,"E92.trimOffspring"),sQuery(id+"F0.wireOp",EDGE,"E93.trimOffspring"),sQuery(id+"F0.wireOp",EDGE,"E94.trimOffspring"),sQuery(id+"F0.wireOp",EDGE,"E95.trimOffspring"),sQuery(id+"F0.wireOp",EDGE,"E96.trimOffspring"),sQuery(id+"F0.wireOp",EDGE,"E97.trimOffspring"),sQuery(id+"F0.wireOp",EDGE,"E98.trimOffspring"),sQuery(id+"F0.wireOp",EDGE,"E99.trimOffspring"),sQuery(id+"F0.wireOp",EDGE,"E100.trimOffspring"),sQuery(id+"F0.wireOp",EDGE,"E101.trimOffspring"),sQuery(id+"F0.wireOp",EDGE,"E102.trimOffspring"),sQuery(id+"F0.wireOp",EDGE,"E103.trimOffspring"),sQuery(id+"F0.wireOp",EDGE,"E104.trimOffspring"),sQuery(id+"F0.wireOp",EDGE,"E105.trimOffspring"),sQuery(id+"F0.wireOp",EDGE,"E106.trimOffspring"),sQuery(id+"F0.wireOp",EDGE,"E107.trimOffspring"),sQuery(id+"F0.wireOp",EDGE,"E108.trimOffspring"),sQuery(id+"F0.wireOp",EDGE,"E109.trimOffspring"),sQuery(id+"F0.wireOp",EDGE,"E110.trimOffspring"),sQuery(id+"F0.wireOp",EDGE,"E111.trimOffspring"),sQuery(id+"F0.wireOp",EDGE,"E112.trimOffspring"),sQuery(id+"F0.wireOp",EDGE,"E113.trimOffspring"),sQuery(id+"F0.wireOp",EDGE,"E114.trimOffspring"),sQuery(id+"F0.wireOp",EDGE,"E115.trimOffspring"),sQuery(id+"F0.wireOp",EDGE,"E116.trimOffspring"),sQuery(id+"F0.wireOp",EDGE,"E117.trimOffspring"),sQuery(id+"F0.wireOp",EDGE,"E118.trimOffspring"),sQuery(id+"F0.wireOp",EDGE,"E119.trimOffspring"),sQuery(id+"F0.wireOp",EDGE,"E120.trimOffspring"),sQuery(id+"F0.wireOp",EDGE,"E121.trimOffspring"),sQuery(id+"F0.wireOp",EDGE,"E122.trimOffspring"),sQuery(id+"F0.wireOp",EDGE,"E123.trimOffspring"),sQuery(id+"F0.wireOp",EDGE,"E124.trimOffspring"),sQuery(id+"F0.wireOp",EDGE,"E125.trimOffspring"),sQuery(id+"F0.wireOp",EDGE,"E126.trimOffspring"),sQuery(id+"F0.wireOp",EDGE,"E127.trimOffspring"),sQuery(id+"F0.wireOp",EDGE,"E128.trimOffspring"),sQuery(id+"F0.wireOp",EDGE,"E129.trimOffspring"),sQuery(id+"F0.wireOp",EDGE,"E130.trimOffspring"),sQuery(id+"F0.wireOp",EDGE,"E131.trimOffspring"),sQuery(id+"F0.wireOp",EDGE,"E132.trimOffspring"),sQuery(id+"F0.wireOp",EDGE,"E133.trimOffspring"),sQuery(id+"F0.wireOp",EDGE,"E134.trimOffspring"),sQuery(id+"F0.wireOp",EDGE,"E135.trimOffspring"),sQuery(id+"F0.wireOp",EDGE,"E136.trimOffspring"),sQuery(id+"F0.wireOp",EDGE,"E137.trimOffspring"),sQuery(id+"F0.wireOp",EDGE,"E138.trimOffspring"),sQuery(id+"F0.wireOp",EDGE,"E139.trimOffspring"),sQuery(id+"F0.wireOp",EDGE,"E140.trimOffspring"),sQuery(id+"F0.wireOp",EDGE,"E141.trimOffspring"),sQuery(id+"F0.wireOp",EDGE,"E142.trimOffspring"),sQuery(id+"F0.wireOp",EDGE,"E143.trimOffspring"),sQuery(id+"F0.wireOp",EDGE,"E144.trimOffspring"),sQuery(id+"F0.wireOp",EDGE,"E145.trimOffspring"),sQuery(id+"F0.wireOp",EDGE,"E146.trimOffspring"),sQuery(id+"F0.wireOp",EDGE,"E147.trimOffspring"),sQuery(id+"F0.wireOp",EDGE,"E148.trimOffspring"),sQuery(id+"F0.wireOp",EDGE,"E149.trimOffspring"),sQuery(id+"F0.wireOp",EDGE,"E150.trimOffspring"),sQuery(id+"F0.wireOp",EDGE,"E151.trimOffspring"),sQuery(id+"F0.wireOp",EDGE,"E152.trimOffspring")])],"isStart":false});
            var sketch = newSketch(context, id + "F2", { "sketchPlane" : qUnion([Q0])});
            skCircle(sketch, "E153", {"center": v(0, 0) * mm, "radius": 1.8 * mm});
            skSolve(sketch);
        }
        {
            var Q0;
            Q0=makeQuery(id+"F2.imprint","IMPRINT",FACE,{"disambiguationData":[TD([[makeQuery(id+"F2.imprint","IMPRINT",EDGE,{"derivedFrom":sQuery(id+"F2.wireOp",EDGE,"E153")}),1.0]])]});
            extrude(context, id + "F3", {"entities" : qUnion([Q0]), "operationType" : NewBodyOperationType.REMOVE, "oppositeDirection" : true, "depth" : 5 * mm});
        }
        {
            var Q0;
            Q0=makeQuery(id+"F1.opExtrude","CAP_FACE",FACE,{"disambiguationData":[OSD([sQuery(id+"F0.wireOp",EDGE,"E0"),sQuery(id+"F0.wireOp",EDGE,"E1"),sQuery(id+"F0.wireOp",EDGE,"E2"),sQuery(id+"F0.wireOp",EDGE,"E3.1.0"),sQuery(id+"F0.wireOp",EDGE,"E3.1.1"),sQuery(id+"F0.wireOp",EDGE,"E3.2.0"),sQuery(id+"F0.wireOp",EDGE,"E3.2.1"),sQuery(id+"F0.wireOp",EDGE,"E3.3.0"),sQuery(id+"F0.wireOp",EDGE,"E3.3.1"),sQuery(id+"F0.wireOp",EDGE,"E3.4.0"),sQuery(id+"F0.wireOp",EDGE,"E3.4.1"),sQuery(id+"F0.wireOp",EDGE,"E3.5.0"),sQuery(id+"F0.wireOp",EDGE,"E3.5.1"),sQuery(id+"F0.wireOp",EDGE,"E3.6.0"),sQuery(id+"F0.wireOp",EDGE,"E3.6.1"),sQuery(id+"F0.wireOp",EDGE,"E3.7.0"),sQuery(id+"F0.wireOp",EDGE,"E3.7.1"),sQuery(id+"F0.wireOp",EDGE,"E3.8.0"),sQuery(id+"F0.wireOp",EDGE,"E3.8.1"),sQuery(id+"F0.wireOp",EDGE,"E3.9.0"),sQuery(id+"F0.wireOp",EDGE,"E3.9.1"),sQuery(id+"F0.wireOp",EDGE,"E3.10.0"),sQuery(id+"F0.wireOp",EDGE,"E3.10.1"),sQuery(id+"F0.wireOp",EDGE,"E3.11.0"),sQuery(id+"F0.wireOp",EDGE,"E3.11.1"),sQuery(id+"F0.wireOp",EDGE,"E3.12.0"),sQuery(id+"F0.wireOp",EDGE,"E3.12.1"),sQuery(id+"F0.wireOp",EDGE,"E3.13.0"),sQuery(id+"F0.wireOp",EDGE,"E3.13.1"),sQuery(id+"F0.wireOp",EDGE,"E3.14.0"),sQuery(id+"F0.wireOp",EDGE,"E3.14.1"),sQuery(id+"F0.wireOp",EDGE,"E3.15.0"),sQuery(id+"F0.wireOp",EDGE,"E3.15.1"),sQuery(id+"F0.wireOp",EDGE,"E3.16.0"),sQuery(id+"F0.wireOp",EDGE,"E3.16.1"),sQuery(id+"F0.wireOp",EDGE,"E3.17.0"),sQuery(id+"F0.wireOp",EDGE,"E3.17.1"),sQuery(id+"F0.wireOp",EDGE,"E3.18.0"),sQuery(id+"F0.wireOp",EDGE,"E3.18.1"),sQuery(id+"F0.wireOp",EDGE,"E3.19.0"),sQuery(id+"F0.wireOp",EDGE,"E3.19.1"),sQuery(id+"F0.wireOp",EDGE,"E3.20.0"),sQuery(id+"F0.wireOp",EDGE,"E3.20.1"),sQuery(id+"F0.wireOp",EDGE,"E3.21.0"),sQuery(id+"F0.wireOp",EDGE,"E3.21.1"),sQuery(id+"F0.wireOp",EDGE,"E3.22.0"),sQuery(id+"F0.wireOp",EDGE,"E3.22.1"),sQuery(id+"F0.wireOp",EDGE,"E3.23.0"),sQuery(id+"F0.wireOp",EDGE,"E3.23.1"),sQuery(id+"F0.wireOp",EDGE,"E3.24.0"),sQuery(id+"F0.wireOp",EDGE,"E3.24.1"),sQuery(id+"F0.wireOp",EDGE,"E3.25.0"),sQuery(id+"F0.wireOp",EDGE,"E3.25.1"),sQuery(id+"F0.wireOp",EDGE,"E3.26.0"),sQuery(id+"F0.wireOp",EDGE,"E3.26.1"),sQuery(id+"F0.wireOp",EDGE,"E3.27.0"),sQuery(id+"F0.wireOp",EDGE,"E3.27.1"),sQuery(id+"F0.wireOp",EDGE,"E3.28.0"),sQuery(id+"F0.wireOp",EDGE,"E3.28.1"),sQuery(id+"F0.wireOp",EDGE,"E3.29.0"),sQuery(id+"F0.wireOp",EDGE,"E3.29.1"),sQuery(id+"F0.wireOp",EDGE,"E3.30.0"),sQuery(id+"F0.wireOp",EDGE,"E3.30.1"),sQuery(id+"F0.wireOp",EDGE,"E3.31.0"),sQuery(id+"F0.wireOp",EDGE,"E3.31.1"),sQuery(id+"F0.wireOp",EDGE,"E3.32.0"),sQuery(id+"F0.wireOp",EDGE,"E3.32.1"),sQuery(id+"F0.wireOp",EDGE,"E3.33.0"),sQuery(id+"F0.wireOp",EDGE,"E3.33.1"),sQuery(id+"F0.wireOp",EDGE,"E3.34.0"),sQuery(id+"F0.wireOp",EDGE,"E3.34.1"),sQuery(id+"F0.wireOp",EDGE,"E3.35.0"),sQuery(id+"F0.wireOp",EDGE,"E3.35.1"),sQuery(id+"F0.wireOp",EDGE,"E3.36.0"),sQuery(id+"F0.wireOp",EDGE,"E3.36.1"),sQuery(id+"F0.wireOp",EDGE,"E3.37.0"),sQuery(id+"F0.wireOp",EDGE,"E3.37.1"),sQuery(id+"F0.wireOp",EDGE,"E3.38.0"),sQuery(id+"F0.wireOp",EDGE,"E3.38.1"),sQuery(id+"F0.wireOp",EDGE,"E3.39.0"),sQuery(id+"F0.wireOp",EDGE,"E3.39.1"),sQuery(id+"F0.wireOp",EDGE,"E3.40.0"),sQuery(id+"F0.wireOp",EDGE,"E3.40.1"),sQuery(id+"F0.wireOp",EDGE,"E3.41.0"),sQuery(id+"F0.wireOp",EDGE,"E3.41.1"),sQuery(id+"F0.wireOp",EDGE,"E3.42.0"),sQuery(id+"F0.wireOp",EDGE,"E3.42.1"),sQuery(id+"F0.wireOp",EDGE,"E3.43.0"),sQuery(id+"F0.wireOp",EDGE,"E3.43.1"),sQuery(id+"F0.wireOp",EDGE,"E3.44.0"),sQuery(id+"F0.wireOp",EDGE,"E3.44.1"),sQuery(id+"F0.wireOp",EDGE,"E3.45.0"),sQuery(id+"F0.wireOp",EDGE,"E3.45.1"),sQuery(id+"F0.wireOp",EDGE,"E3.46.0"),sQuery(id+"F0.wireOp",EDGE,"E3.46.1"),sQuery(id+"F0.wireOp",EDGE,"E3.47.0"),sQuery(id+"F0.wireOp",EDGE,"E3.47.1"),sQuery(id+"F0.wireOp",EDGE,"E3.48.0"),sQuery(id+"F0.wireOp",EDGE,"E3.48.1"),sQuery(id+"F0.wireOp",EDGE,"E3.49.0"),sQuery(id+"F0.wireOp",EDGE,"E3.49.1"),sQuery(id+"F0.wireOp",EDGE,"E3.50.0"),sQuery(id+"F0.wireOp",EDGE,"E3.50.1"),sQuery(id+"F0.wireOp",EDGE,"E3.51.0"),sQuery(id+"F0.wireOp",EDGE,"E3.51.1"),sQuery(id+"F0.wireOp",EDGE,"E3.52.0"),sQuery(id+"F0.wireOp",EDGE,"E3.52.1"),sQuery(id+"F0.wireOp",EDGE,"E3.53.0"),sQuery(id+"F0.wireOp",EDGE,"E3.53.1"),sQuery(id+"F0.wireOp",EDGE,"E3.54.0"),sQuery(id+"F0.wireOp",EDGE,"E3.54.1"),sQuery(id+"F0.wireOp",EDGE,"E3.55.0"),sQuery(id+"F0.wireOp",EDGE,"E3.55.1"),sQuery(id+"F0.wireOp",EDGE,"E3.56.0"),sQuery(id+"F0.wireOp",EDGE,"E3.56.1"),sQuery(id+"F0.wireOp",EDGE,"E3.57.0"),sQuery(id+"F0.wireOp",EDGE,"E3.57.1"),sQuery(id+"F0.wireOp",EDGE,"E3.58.0"),sQuery(id+"F0.wireOp",EDGE,"E3.58.1"),sQuery(id+"F0.wireOp",EDGE,"E3.59.0"),sQuery(id+"F0.wireOp",EDGE,"E3.59.1"),sQuery(id+"F0.wireOp",EDGE,"E3.60.0"),sQuery(id+"F0.wireOp",EDGE,"E3.60.1"),sQuery(id+"F0.wireOp",EDGE,"E3.61.0"),sQuery(id+"F0.wireOp",EDGE,"E3.61.1"),sQuery(id+"F0.wireOp",EDGE,"E3.62.0"),sQuery(id+"F0.wireOp",EDGE,"E3.62.1"),sQuery(id+"F0.wireOp",EDGE,"E3.63.0"),sQuery(id+"F0.wireOp",EDGE,"E3.63.1"),sQuery(id+"F0.wireOp",EDGE,"E3.64.0"),sQuery(id+"F0.wireOp",EDGE,"E3.64.1"),sQuery(id+"F0.wireOp",EDGE,"E3.65.0"),sQuery(id+"F0.wireOp",EDGE,"E3.65.1"),sQuery(id+"F0.wireOp",EDGE,"E3.66.0"),sQuery(id+"F0.wireOp",EDGE,"E3.66.1"),sQuery(id+"F0.wireOp",EDGE,"E3.67.0"),sQuery(id+"F0.wireOp",EDGE,"E3.67.1"),sQuery(id+"F0.wireOp",EDGE,"E3.68.0"),sQuery(id+"F0.wireOp",EDGE,"E3.68.1"),sQuery(id+"F0.wireOp",EDGE,"E3.69.0"),sQuery(id+"F0.wireOp",EDGE,"E3.69.1"),sQuery(id+"F0.wireOp",EDGE,"E3.70.0"),sQuery(id+"F0.wireOp",EDGE,"E3.70.1"),sQuery(id+"F0.wireOp",EDGE,"E3.71.0"),sQuery(id+"F0.wireOp",EDGE,"E3.71.1"),sQuery(id+"F0.wireOp",EDGE,"E3.72.0"),sQuery(id+"F0.wireOp",EDGE,"E3.72.1"),sQuery(id+"F0.wireOp",EDGE,"E3.73.0"),sQuery(id+"F0.wireOp",EDGE,"E3.73.1"),sQuery(id+"F0.wireOp",EDGE,"E3.74.0"),sQuery(id+"F0.wireOp",EDGE,"E3.74.1"),sQuery(id+"F0.wireOp",EDGE,"E3.75.0"),sQuery(id+"F0.wireOp",EDGE,"E3.75.1"),sQuery(id+"F0.wireOp",EDGE,"E3.76.0"),sQuery(id+"F0.wireOp",EDGE,"E3.76.1"),sQuery(id+"F0.wireOp",EDGE,"E3.77.0"),sQuery(id+"F0.wireOp",EDGE,"E3.77.1"),sQuery(id+"F0.wireOp",EDGE,"E3.78.0"),sQuery(id+"F0.wireOp",EDGE,"E3.78.1"),sQuery(id+"F0.wireOp",EDGE,"E3.79.0"),sQuery(id+"F0.wireOp",EDGE,"E3.79.1"),sQuery(id+"F0.wireOp",EDGE,"E3.80.0"),sQuery(id+"F0.wireOp",EDGE,"E3.80.1"),sQuery(id+"F0.wireOp",EDGE,"E3.81.0"),sQuery(id+"F0.wireOp",EDGE,"E3.81.1"),sQuery(id+"F0.wireOp",EDGE,"E3.82.0"),sQuery(id+"F0.wireOp",EDGE,"E3.82.1"),sQuery(id+"F0.wireOp",EDGE,"E3.83.0"),sQuery(id+"F0.wireOp",EDGE,"E3.83.1"),sQuery(id+"F0.wireOp",EDGE,"E3.84.0"),sQuery(id+"F0.wireOp",EDGE,"E3.84.1"),sQuery(id+"F0.wireOp",EDGE,"E3.85.0"),sQuery(id+"F0.wireOp",EDGE,"E3.85.1"),sQuery(id+"F0.wireOp",EDGE,"E3.86.0"),sQuery(id+"F0.wireOp",EDGE,"E3.86.1"),sQuery(id+"F0.wireOp",EDGE,"E3.87.0"),sQuery(id+"F0.wireOp",EDGE,"E3.87.1"),sQuery(id+"F0.wireOp",EDGE,"E3.88.0"),sQuery(id+"F0.wireOp",EDGE,"E3.88.1"),sQuery(id+"F0.wireOp",EDGE,"E3.89.0"),sQuery(id+"F0.wireOp",EDGE,"E3.89.1"),sQuery(id+"F0.wireOp",EDGE,"E3.90.0"),sQuery(id+"F0.wireOp",EDGE,"E3.90.1"),sQuery(id+"F0.wireOp",EDGE,"E3.91.0"),sQuery(id+"F0.wireOp",EDGE,"E3.91.1"),sQuery(id+"F0.wireOp",EDGE,"E3.92.0"),sQuery(id+"F0.wireOp",EDGE,"E3.92.1"),sQuery(id+"F0.wireOp",EDGE,"E3.93.0"),sQuery(id+"F0.wireOp",EDGE,"E3.93.1"),sQuery(id+"F0.wireOp",EDGE,"E3.94.0"),sQuery(id+"F0.wireOp",EDGE,"E3.94.1"),sQuery(id+"F0.wireOp",EDGE,"E3.95.0"),sQuery(id+"F0.wireOp",EDGE,"E3.95.1"),sQuery(id+"F0.wireOp",EDGE,"E3.96.0"),sQuery(id+"F0.wireOp",EDGE,"E3.96.1"),sQuery(id+"F0.wireOp",EDGE,"E3.97.0"),sQuery(id+"F0.wireOp",EDGE,"E3.97.1"),sQuery(id+"F0.wireOp",EDGE,"E3.98.0"),sQuery(id+"F0.wireOp",EDGE,"E3.98.1"),sQuery(id+"F0.wireOp",EDGE,"E3.99.0"),sQuery(id+"F0.wireOp",EDGE,"E3.99.1"),sQuery(id+"F0.wireOp",EDGE,"E3.100.0"),sQuery(id+"F0.wireOp",EDGE,"E3.100.1"),sQuery(id+"F0.wireOp",EDGE,"E3.101.0"),sQuery(id+"F0.wireOp",EDGE,"E3.101.1"),sQuery(id+"F0.wireOp",EDGE,"E3.102.0"),sQuery(id+"F0.wireOp",EDGE,"E3.102.1"),sQuery(id+"F0.wireOp",EDGE,"E3.103.0"),sQuery(id+"F0.wireOp",EDGE,"E3.103.1"),sQuery(id+"F0.wireOp",EDGE,"E3.104.0"),sQuery(id+"F0.wireOp",EDGE,"E3.104.1"),sQuery(id+"F0.wireOp",EDGE,"E3.105.0"),sQuery(id+"F0.wireOp",EDGE,"E3.105.1"),sQuery(id+"F0.wireOp",EDGE,"E3.106.0"),sQuery(id+"F0.wireOp",EDGE,"E3.106.1"),sQuery(id+"F0.wireOp",EDGE,"E3.107.0"),sQuery(id+"F0.wireOp",EDGE,"E3.107.1"),sQuery(id+"F0.wireOp",EDGE,"E3.108.0"),sQuery(id+"F0.wireOp",EDGE,"E3.108.1"),sQuery(id+"F0.wireOp",EDGE,"E3.109.0"),sQuery(id+"F0.wireOp",EDGE,"E3.109.1"),sQuery(id+"F0.wireOp",EDGE,"E3.110.0"),sQuery(id+"F0.wireOp",EDGE,"E3.110.1"),sQuery(id+"F0.wireOp",EDGE,"E3.111.0"),sQuery(id+"F0.wireOp",EDGE,"E3.111.1"),sQuery(id+"F0.wireOp",EDGE,"E3.112.0"),sQuery(id+"F0.wireOp",EDGE,"E3.112.1"),sQuery(id+"F0.wireOp",EDGE,"E3.113.0"),sQuery(id+"F0.wireOp",EDGE,"E3.113.1"),sQuery(id+"F0.wireOp",EDGE,"E3.114.0"),sQuery(id+"F0.wireOp",EDGE,"E3.114.1"),sQuery(id+"F0.wireOp",EDGE,"E3.115.0"),sQuery(id+"F0.wireOp",EDGE,"E3.115.1"),sQuery(id+"F0.wireOp",EDGE,"E3.116.0"),sQuery(id+"F0.wireOp",EDGE,"E3.116.1"),sQuery(id+"F0.wireOp",EDGE,"E3.117.0"),sQuery(id+"F0.wireOp",EDGE,"E3.117.1"),sQuery(id+"F0.wireOp",EDGE,"E3.118.0"),sQuery(id+"F0.wireOp",EDGE,"E3.118.1"),sQuery(id+"F0.wireOp",EDGE,"E3.119.0"),sQuery(id+"F0.wireOp",EDGE,"E3.119.1"),sQuery(id+"F0.wireOp",EDGE,"E3.120.0"),sQuery(id+"F0.wireOp",EDGE,"E3.120.1"),sQuery(id+"F0.wireOp",EDGE,"E3.121.0"),sQuery(id+"F0.wireOp",EDGE,"E3.121.1"),sQuery(id+"F0.wireOp",EDGE,"E3.122.0"),sQuery(id+"F0.wireOp",EDGE,"E3.122.1"),sQuery(id+"F0.wireOp",EDGE,"E3.123.0"),sQuery(id+"F0.wireOp",EDGE,"E3.123.1"),sQuery(id+"F0.wireOp",EDGE,"E3.124.0"),sQuery(id+"F0.wireOp",EDGE,"E3.124.1"),sQuery(id+"F0.wireOp",EDGE,"E3.125.0"),sQuery(id+"F0.wireOp",EDGE,"E3.125.1"),sQuery(id+"F0.wireOp",EDGE,"E3.126.0"),sQuery(id+"F0.wireOp",EDGE,"E3.126.1"),sQuery(id+"F0.wireOp",EDGE,"E3.127.0"),sQuery(id+"F0.wireOp",EDGE,"E3.127.1"),sQuery(id+"F0.wireOp",EDGE,"E3.128.0"),sQuery(id+"F0.wireOp",EDGE,"E3.128.1"),sQuery(id+"F0.wireOp",EDGE,"E3.129.0"),sQuery(id+"F0.wireOp",EDGE,"E3.129.1"),sQuery(id+"F0.wireOp",EDGE,"E3.130.0"),sQuery(id+"F0.wireOp",EDGE,"E3.130.1"),sQuery(id+"F0.wireOp",EDGE,"E3.131.0"),sQuery(id+"F0.wireOp",EDGE,"E3.131.1"),sQuery(id+"F0.wireOp",EDGE,"E3.132.0"),sQuery(id+"F0.wireOp",EDGE,"E3.132.1"),sQuery(id+"F0.wireOp",EDGE,"E3.133.0"),sQuery(id+"F0.wireOp",EDGE,"E3.133.1"),sQuery(id+"F0.wireOp",EDGE,"E3.134.0"),sQuery(id+"F0.wireOp",EDGE,"E3.134.1"),sQuery(id+"F0.wireOp",EDGE,"E3.135.0"),sQuery(id+"F0.wireOp",EDGE,"E3.135.1"),sQuery(id+"F0.wireOp",EDGE,"E3.136.0"),sQuery(id+"F0.wireOp",EDGE,"E3.136.1"),sQuery(id+"F0.wireOp",EDGE,"E3.137.0"),sQuery(id+"F0.wireOp",EDGE,"E3.137.1"),sQuery(id+"F0.wireOp",EDGE,"E3.138.0"),sQuery(id+"F0.wireOp",EDGE,"E3.138.1"),sQuery(id+"F0.wireOp",EDGE,"E3.139.0"),sQuery(id+"F0.wireOp",EDGE,"E3.139.1"),sQuery(id+"F0.wireOp",EDGE,"E3.140.0"),sQuery(id+"F0.wireOp",EDGE,"E3.140.1"),sQuery(id+"F0.wireOp",EDGE,"E3.141.0"),sQuery(id+"F0.wireOp",EDGE,"E3.141.1"),sQuery(id+"F0.wireOp",EDGE,"E3.142.0"),sQuery(id+"F0.wireOp",EDGE,"E3.142.1"),sQuery(id+"F0.wireOp",EDGE,"E3.143.0"),sQuery(id+"F0.wireOp",EDGE,"E3.143.1"),sQuery(id+"F0.wireOp",EDGE,"E3.144.0"),sQuery(id+"F0.wireOp",EDGE,"E3.144.1"),sQuery(id+"F0.wireOp",EDGE,"E3.145.0"),sQuery(id+"F0.wireOp",EDGE,"E3.145.1"),sQuery(id+"F0.wireOp",EDGE,"E3.146.0"),sQuery(id+"F0.wireOp",EDGE,"E3.146.1"),sQuery(id+"F0.wireOp",EDGE,"E3.147.0"),sQuery(id+"F0.wireOp",EDGE,"E3.147.1"),sQuery(id+"F0.wireOp",EDGE,"E3.148.0"),sQuery(id+"F0.wireOp",EDGE,"E3.148.1"),sQuery(id+"F0.wireOp",EDGE,"E3.149.0"),sQuery(id+"F0.wireOp",EDGE,"E3.149.1"),sQuery(id+"F0.wireOp",EDGE,"E4.trimOffspring"),sQuery(id+"F0.wireOp",EDGE,"E5.trimOffspring"),sQuery(id+"F0.wireOp",EDGE,"E6.trimOffspring"),sQuery(id+"F0.wireOp",EDGE,"E7.trimOffspring"),sQuery(id+"F0.wireOp",EDGE,"E8.trimOffspring"),sQuery(id+"F0.wireOp",EDGE,"E9.trimOffspring"),sQuery(id+"F0.wireOp",EDGE,"E10.trimOffspring"),sQuery(id+"F0.wireOp",EDGE,"E11.trimOffspring"),sQuery(id+"F0.wireOp",EDGE,"E12.trimOffspring"),sQuery(id+"F0.wireOp",EDGE,"E13.trimOffspring"),sQuery(id+"F0.wireOp",EDGE,"E14.trimOffspring"),sQuery(id+"F0.wireOp",EDGE,"E15.trimOffspring"),sQuery(id+"F0.wireOp",EDGE,"E16.trimOffspring"),sQuery(id+"F0.wireOp",EDGE,"E17.trimOffspring"),sQuery(id+"F0.wireOp",EDGE,"E18.trimOffspring"),sQuery(id+"F0.wireOp",EDGE,"E19.trimOffspring"),sQuery(id+"F0.wireOp",EDGE,"E20.trimOffspring"),sQuery(id+"F0.wireOp",EDGE,"E21.trimOffspring"),sQuery(id+"F0.wireOp",EDGE,"E22.trimOffspring"),sQuery(id+"F0.wireOp",EDGE,"E23.trimOffspring"),sQuery(id+"F0.wireOp",EDGE,"E24.trimOffspring"),sQuery(id+"F0.wireOp",EDGE,"E25.trimOffspring"),sQuery(id+"F0.wireOp",EDGE,"E26.trimOffspring"),sQuery(id+"F0.wireOp",EDGE,"E27.trimOffspring"),sQuery(id+"F0.wireOp",EDGE,"E28.trimOffspring"),sQuery(id+"F0.wireOp",EDGE,"E29.trimOffspring"),sQuery(id+"F0.wireOp",EDGE,"E30.trimOffspring"),sQuery(id+"F0.wireOp",EDGE,"E31.trimOffspring"),sQuery(id+"F0.wireOp",EDGE,"E32.trimOffspring"),sQuery(id+"F0.wireOp",EDGE,"E33.trimOffspring"),sQuery(id+"F0.wireOp",EDGE,"E34.trimOffspring"),sQuery(id+"F0.wireOp",EDGE,"E35.trimOffspring"),sQuery(id+"F0.wireOp",EDGE,"E36.trimOffspring"),sQuery(id+"F0.wireOp",EDGE,"E37.trimOffspring"),sQuery(id+"F0.wireOp",EDGE,"E38.trimOffspring"),sQuery(id+"F0.wireOp",EDGE,"E39.trimOffspring"),sQuery(id+"F0.wireOp",EDGE,"E40.trimOffspring"),sQuery(id+"F0.wireOp",EDGE,"E41.trimOffspring"),sQuery(id+"F0.wireOp",EDGE,"E42.trimOffspring"),sQuery(id+"F0.wireOp",EDGE,"E43.trimOffspring"),sQuery(id+"F0.wireOp",EDGE,"E44.trimOffspring"),sQuery(id+"F0.wireOp",EDGE,"E45.trimOffspring"),sQuery(id+"F0.wireOp",EDGE,"E46.trimOffspring"),sQuery(id+"F0.wireOp",EDGE,"E47.trimOffspring"),sQuery(id+"F0.wireOp",EDGE,"E48.trimOffspring"),sQuery(id+"F0.wireOp",EDGE,"E49.trimOffspring"),sQuery(id+"F0.wireOp",EDGE,"E50.trimOffspring"),sQuery(id+"F0.wireOp",EDGE,"E51.trimOffspring"),sQuery(id+"F0.wireOp",EDGE,"E52.trimOffspring"),sQuery(id+"F0.wireOp",EDGE,"E53.trimOffspring"),sQuery(id+"F0.wireOp",EDGE,"E54.trimOffspring"),sQuery(id+"F0.wireOp",EDGE,"E55.trimOffspring"),sQuery(id+"F0.wireOp",EDGE,"E56.trimOffspring"),sQuery(id+"F0.wireOp",EDGE,"E57.trimOffspring"),sQuery(id+"F0.wireOp",EDGE,"E58.trimOffspring"),sQuery(id+"F0.wireOp",EDGE,"E59.trimOffspring"),sQuery(id+"F0.wireOp",EDGE,"E60.trimOffspring"),sQuery(id+"F0.wireOp",EDGE,"E61.trimOffspring"),sQuery(id+"F0.wireOp",EDGE,"E62.trimOffspring"),sQuery(id+"F0.wireOp",EDGE,"E63.trimOffspring"),sQuery(id+"F0.wireOp",EDGE,"E64.trimOffspring"),sQuery(id+"F0.wireOp",EDGE,"E65.trimOffspring"),sQuery(id+"F0.wireOp",EDGE,"E66.trimOffspring"),sQuery(id+"F0.wireOp",EDGE,"E67.trimOffspring"),sQuery(id+"F0.wireOp",EDGE,"E68.trimOffspring"),sQuery(id+"F0.wireOp",EDGE,"E69.trimOffspring"),sQuery(id+"F0.wireOp",EDGE,"E70.trimOffspring"),sQuery(id+"F0.wireOp",EDGE,"E71.trimOffspring"),sQuery(id+"F0.wireOp",EDGE,"E72.trimOffspring"),sQuery(id+"F0.wireOp",EDGE,"E73.trimOffspring"),sQuery(id+"F0.wireOp",EDGE,"E74.trimOffspring"),sQuery(id+"F0.wireOp",EDGE,"E75.trimOffspring"),sQuery(id+"F0.wireOp",EDGE,"E76.trimOffspring"),sQuery(id+"F0.wireOp",EDGE,"E77.trimOffspring"),sQuery(id+"F0.wireOp",EDGE,"E78.trimOffspring"),sQuery(id+"F0.wireOp",EDGE,"E79.trimOffspring"),sQuery(id+"F0.wireOp",EDGE,"E80.trimOffspring"),sQuery(id+"F0.wireOp",EDGE,"E81.trimOffspring"),sQuery(id+"F0.wireOp",EDGE,"E82.trimOffspring"),sQuery(id+"F0.wireOp",EDGE,"E83.trimOffspring"),sQuery(id+"F0.wireOp",EDGE,"E84.trimOffspring"),sQuery(id+"F0.wireOp",EDGE,"E85.trimOffspring"),sQuery(id+"F0.wireOp",EDGE,"E86.trimOffspring"),sQuery(id+"F0.wireOp",EDGE,"E87.trimOffspring"),sQuery(id+"F0.wireOp",EDGE,"E88.trimOffspring"),sQuery(id+"F0.wireOp",EDGE,"E89.trimOffspring"),sQuery(id+"F0.wireOp",EDGE,"E90.trimOffspring"),sQuery(id+"F0.wireOp",EDGE,"E91.trimOffspring"),sQuery(id+"F0.wireOp",EDGE,"E92.trimOffspring"),sQuery(id+"F0.wireOp",EDGE,"E93.trimOffspring"),sQuery(id+"F0.wireOp",EDGE,"E94.trimOffspring"),sQuery(id+"F0.wireOp",EDGE,"E95.trimOffspring"),sQuery(id+"F0.wireOp",EDGE,"E96.trimOffspring"),sQuery(id+"F0.wireOp",EDGE,"E97.trimOffspring"),sQuery(id+"F0.wireOp",EDGE,"E98.trimOffspring"),sQuery(id+"F0.wireOp",EDGE,"E99.trimOffspring"),sQuery(id+"F0.wireOp",EDGE,"E100.trimOffspring"),sQuery(id+"F0.wireOp",EDGE,"E101.trimOffspring"),sQuery(id+"F0.wireOp",EDGE,"E102.trimOffspring"),sQuery(id+"F0.wireOp",EDGE,"E103.trimOffspring"),sQuery(id+"F0.wireOp",EDGE,"E104.trimOffspring"),sQuery(id+"F0.wireOp",EDGE,"E105.trimOffspring"),sQuery(id+"F0.wireOp",EDGE,"E106.trimOffspring"),sQuery(id+"F0.wireOp",EDGE,"E107.trimOffspring"),sQuery(id+"F0.wireOp",EDGE,"E108.trimOffspring"),sQuery(id+"F0.wireOp",EDGE,"E109.trimOffspring"),sQuery(id+"F0.wireOp",EDGE,"E110.trimOffspring"),sQuery(id+"F0.wireOp",EDGE,"E111.trimOffspring"),sQuery(id+"F0.wireOp",EDGE,"E112.trimOffspring"),sQuery(id+"F0.wireOp",EDGE,"E113.trimOffspring"),sQuery(id+"F0.wireOp",EDGE,"E114.trimOffspring"),sQuery(id+"F0.wireOp",EDGE,"E115.trimOffspring"),sQuery(id+"F0.wireOp",EDGE,"E116.trimOffspring"),sQuery(id+"F0.wireOp",EDGE,"E117.trimOffspring"),sQuery(id+"F0.wireOp",EDGE,"E118.trimOffspring"),sQuery(id+"F0.wireOp",EDGE,"E119.trimOffspring"),sQuery(id+"F0.wireOp",EDGE,"E120.trimOffspring"),sQuery(id+"F0.wireOp",EDGE,"E121.trimOffspring"),sQuery(id+"F0.wireOp",EDGE,"E122.trimOffspring"),sQuery(id+"F0.wireOp",EDGE,"E123.trimOffspring"),sQuery(id+"F0.wireOp",EDGE,"E124.trimOffspring"),sQuery(id+"F0.wireOp",EDGE,"E125.trimOffspring"),sQuery(id+"F0.wireOp",EDGE,"E126.trimOffspring"),sQuery(id+"F0.wireOp",EDGE,"E127.trimOffspring"),sQuery(id+"F0.wireOp",EDGE,"E128.trimOffspring"),sQuery(id+"F0.wireOp",EDGE,"E129.trimOffspring"),sQuery(id+"F0.wireOp",EDGE,"E130.trimOffspring"),sQuery(id+"F0.wireOp",EDGE,"E131.trimOffspring"),sQuery(id+"F0.wireOp",EDGE,"E132.trimOffspring"),sQuery(id+"F0.wireOp",EDGE,"E133.trimOffspring"),sQuery(id+"F0.wireOp",EDGE,"E134.trimOffspring"),sQuery(id+"F0.wireOp",EDGE,"E135.trimOffspring"),sQuery(id+"F0.wireOp",EDGE,"E136.trimOffspring"),sQuery(id+"F0.wireOp",EDGE,"E137.trimOffspring"),sQuery(id+"F0.wireOp",EDGE,"E138.trimOffspring"),sQuery(id+"F0.wireOp",EDGE,"E139.trimOffspring"),sQuery(id+"F0.wireOp",EDGE,"E140.trimOffspring"),sQuery(id+"F0.wireOp",EDGE,"E141.trimOffspring"),sQuery(id+"F0.wireOp",EDGE,"E142.trimOffspring"),sQuery(id+"F0.wireOp",EDGE,"E143.trimOffspring"),sQuery(id+"F0.wireOp",EDGE,"E144.trimOffspring"),sQuery(id+"F0.wireOp",EDGE,"E145.trimOffspring"),sQuery(id+"F0.wireOp",EDGE,"E146.trimOffspring"),sQuery(id+"F0.wireOp",EDGE,"E147.trimOffspring"),sQuery(id+"F0.wireOp",EDGE,"E148.trimOffspring"),sQuery(id+"F0.wireOp",EDGE,"E149.trimOffspring"),sQuery(id+"F0.wireOp",EDGE,"E150.trimOffspring"),sQuery(id+"F0.wireOp",EDGE,"E151.trimOffspring"),sQuery(id+"F0.wireOp",EDGE,"E152.trimOffspring")])],"isStart":true});
            var sketch = newSketch(context, id + "F4", { "sketchPlane" : qUnion([Q0])});
            skLineSegment(sketch, "E154", {"start": v(-2, -1.1) * mm, "end": v(2, -1.1) * mm});
            skLineSegment(sketch, "E155", {"start": v(2, -1.1) * mm, "end": v(0, 3.57) * mm});
            skLineSegment(sketch, "E156", {"start": v(0, 3.57) * mm, "end": v(-2, -1.1) * mm});
            skSolve(sketch);
        }
        {
            var Q0;
            Q0=makeQuery(id+"F4.imprint","IMPRINT",FACE,{"disambiguationData":[TD([[makeQuery(id+"F4.imprint","IMPRINT",EDGE,{"derivedFrom":sQuery(id+"F4.wireOp",EDGE,"E154")}),1.0]])]});
            extrude(context, id + "F5", {"entities" : qUnion([Q0]), "operationType" : NewBodyOperationType.REMOVE, "oppositeDirection" : true, "depth" : 1 * mm});
        }
    });
